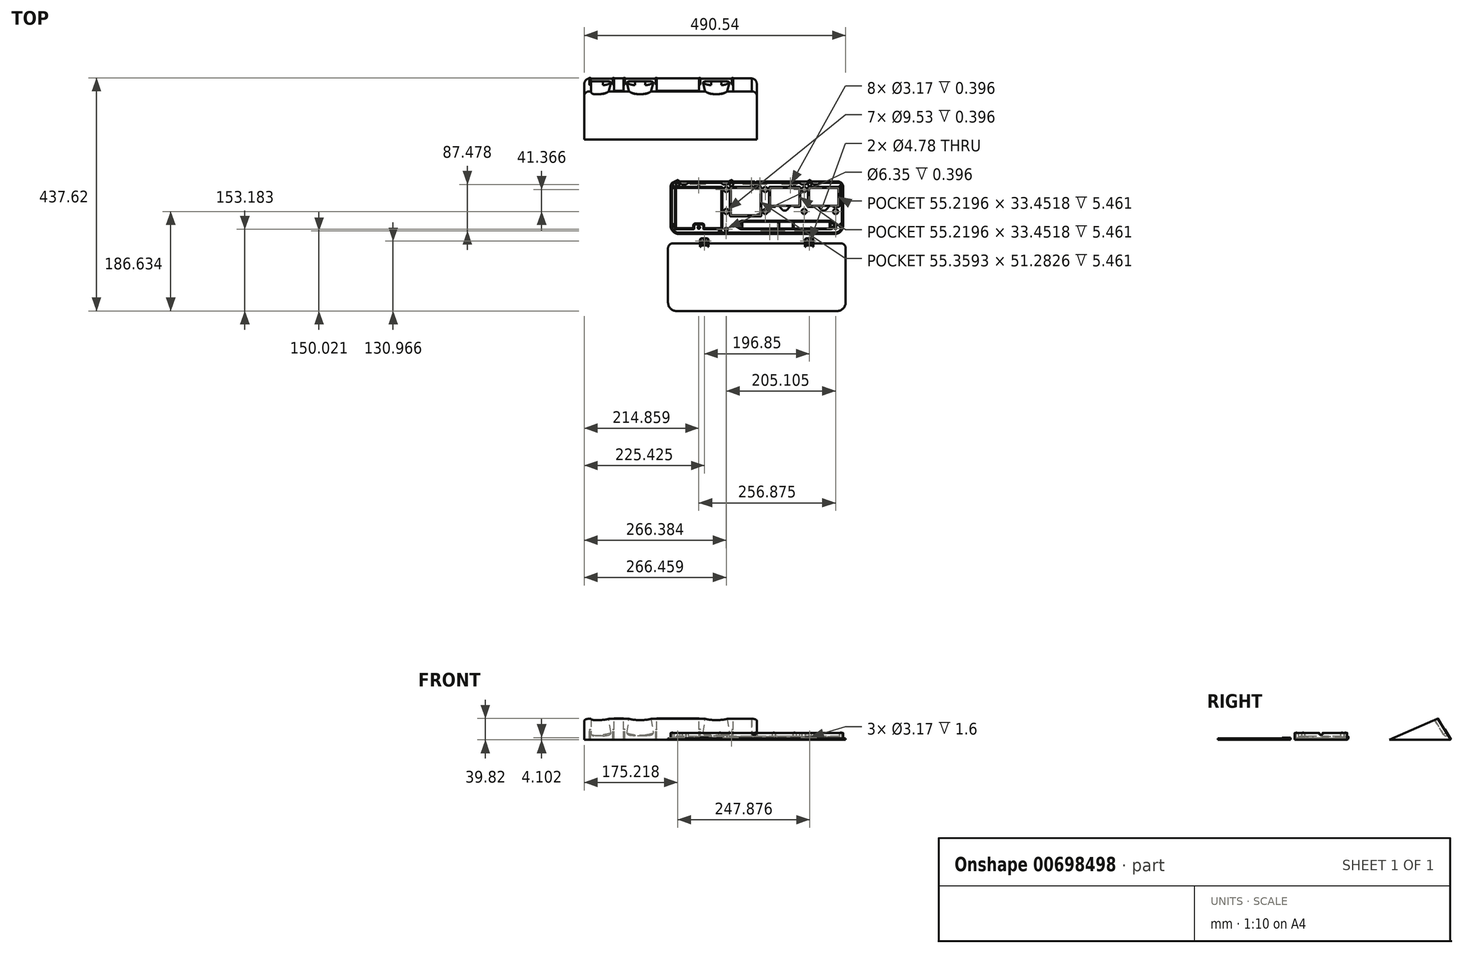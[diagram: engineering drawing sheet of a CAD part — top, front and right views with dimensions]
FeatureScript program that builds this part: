
annotation { "Feature Type Name" : "Feature", "Feature Type Description" : "" }
export const myFeature = defineFeature(function(context is Context, id is Id, definition is map)
    precondition{}
    {
        {
            var Q0;
            Q0=qCreatedBy(makeId("Top.planeOp"),FACE);
            var sketch = newSketch(context, id + "F0", { "sketchPlane" : qUnion([Q0])});
            skLineSegment(sketch, "E0.bottom", {"start": v(161.93, -49.21) * mm, "end": v(-161.93, -49.21) * mm});
            skLineSegment(sketch, "E0.top", {"start": v(161.93, 49.21) * mm, "end": v(-161.93, 49.21) * mm});
            skLineSegment(sketch, "E0.left", {"start": v(161.93, -49.21) * mm, "end": v(161.93, 49.21) * mm});
            skLineSegment(sketch, "E0.right", {"start": v(-161.93, -49.21) * mm, "end": v(-161.93, 49.21) * mm});
            skPoint(sketch, "E0.middle", {"position": v(0, 0) * mm});
            skSolve(sketch);
        }
        {
            var Q0;
            Q0=makeQuery(id+"F0.imprint","IMPRINT",FACE,{"disambiguationData":[TD([[makeQuery(id+"F0.imprint","IMPRINT",EDGE,{"derivedFrom":sQuery(id+"F0.wireOp",EDGE,"E0.bottom")}),-1.0]])]});
            extrude(context, id + "F1", {"entities" : qUnion([Q0]), "depth" : 3.17 * mm, "offsetDistance" : 25.4 * mm});
        }
        {
            var Q0;
            Q0=makeQuery(id+"F1.opExtrude","SWEPT_EDGE",EDGE,{"disambiguationData":[OSD([sQuery(id+"F0.wireOp",EDGE,"E0.bottom"),sQuery(id+"F0.wireOp",EDGE,"E0.right")])]});
            var Q1;
            Q1=makeQuery(id+"F1.opExtrude","SWEPT_EDGE",EDGE,{"disambiguationData":[OSD([sQuery(id+"F0.wireOp",EDGE,"E0.bottom"),sQuery(id+"F0.wireOp",EDGE,"E0.left")])]});
            fillet(context, id + "F2", {"entities" : qUnion([Q0, Q1]), "radius" : 15.88 * mm, "tangentPropagation" : true, "allowEdgeOverflow" : false});
        }
        {
            var Q0;
            Q0=makeQuery(id+"F1.opExtrude","SWEPT_EDGE",EDGE,{"disambiguationData":[OSD([sQuery(id+"F0.wireOp",EDGE,"E0.top"),sQuery(id+"F0.wireOp",EDGE,"E0.right")])]});
            var Q1;
            Q1=makeQuery(id+"F1.opExtrude","SWEPT_EDGE",EDGE,{"disambiguationData":[OSD([sQuery(id+"F0.wireOp",EDGE,"E0.top"),sQuery(id+"F0.wireOp",EDGE,"E0.left")])]});
            fillet(context, id + "F3", {"entities" : qUnion([Q0, Q1]), "radius" : 9.52 * mm, "tangentPropagation" : true, "allowEdgeOverflow" : false});
        }
        {
            var Q0;
            Q0=makeQuery(id+"F1.opExtrude","CAP_FACE",FACE,{"disambiguationData":[OSD([sQuery(id+"F0.wireOp",EDGE,"E0.bottom"),sQuery(id+"F0.wireOp",EDGE,"E0.top"),sQuery(id+"F0.wireOp",EDGE,"E0.left"),sQuery(id+"F0.wireOp",EDGE,"E0.right")])],"isStart":false});
            var sketch = newSketch(context, id + "F4", { "sketchPlane" : qUnion([Q0])});
            skArc(sketch, "E1.0", {"start": v(-152.4, 46.93) * mm, "mid": v(-157.52, 44.8) * mm, "end": v(-159.64, 39.69) * mm});
            skArc(sketch, "E2.0", {"start": v(-159.64, -33.34) * mm, "mid": v(-155.66, -42.95) * mm, "end": v(-146.05, -46.93) * mm});
            skLineSegment(sketch, "E3.0", {"start": v(-159.64, -33.34) * mm, "end": v(-159.64, 39.69) * mm});
            skArc(sketch, "E4.0", {"start": v(146.05, -46.93) * mm, "mid": v(155.66, -42.95) * mm, "end": v(159.64, -33.34) * mm});
            skArc(sketch, "E5.0", {"start": v(159.64, 39.69) * mm, "mid": v(157.52, 44.8) * mm, "end": v(152.4, 46.93) * mm});
            skLineSegment(sketch, "E6.0", {"start": v(159.64, -33.34) * mm, "end": v(159.64, 39.69) * mm});
            skLineSegment(sketch, "E7.0", {"start": v(152.4, 46.93) * mm, "end": v(-152.4, 46.93) * mm});
            skLineSegment(sketch, "E8.0", {"start": v(146.05, -46.93) * mm, "end": v(-146.05, -46.93) * mm});
            skSolve(sketch);
        }
        {
            var Q0;
            Q0=makeQuery(id+"F4.imprint","IMPRINT",FACE,{"disambiguationData":[TD([[makeQuery(id+"F4.imprint","IMPRINT",EDGE,{"derivedFrom":sQuery(id+"F4.wireOp",EDGE,"E1.0")}),-1.0]])]});
            extrude(context, id + "F5", {"entities" : qUnion([Q0]), "operationType" : NewBodyOperationType.ADD, "depth" : 9.52 * mm, "offsetDistance" : 25.4 * mm});
        }
        {
            var Q0;
            Q0=makeQuery(id+"F1.opExtrude","CAP_FACE",FACE,{"disambiguationData":[OSD([sQuery(id+"F0.wireOp",EDGE,"E0.bottom"),sQuery(id+"F0.wireOp",EDGE,"E0.top"),sQuery(id+"F0.wireOp",EDGE,"E0.left"),sQuery(id+"F0.wireOp",EDGE,"E0.right")])],"isStart":false});
            var sketch = newSketch(context, id + "F6", { "sketchPlane" : qUnion([Q0])});
            skCircle(sketch, "E9", {"center": v(-158.52, -33.34) * mm, "radius": 3.18 * mm});
            skLineSegment(sketch, "E10", {"start": v(-158.52, -33.34) * mm, "end": v(-158.52, 39.69) * mm, "construction": true});
            skCircle(sketch, "E11", {"center": v(-158.52, 39.69) * mm, "radius": 3.18 * mm});
            skCircle(sketch, "E12", {"center": v(158.23, 39.4) * mm, "radius": 3.18 * mm});
            skCircle(sketch, "E13", {"center": v(157.67, -33.34) * mm, "radius": 3.18 * mm});
            skCircle(sketch, "E14", {"center": v(70.74, 45.8) * mm, "radius": 3.18 * mm});
            skCircle(sketch, "E15", {"center": v(-2.29, 45.8) * mm, "radius": 3.29 * mm});
            skCircle(sketch, "E16", {"center": v(31.57, -45.8) * mm, "radius": 3.18 * mm});
            skCircle(sketch, "E17", {"center": v(-68.96, -45.8) * mm, "radius": 3.18 * mm});
            skSolve(sketch);
        }
        {
            var Q0;
            {var subQ0=sQuery(id+"F6.wireOp",EDGE,"E9");var subQ1=makeQuery(id+"F5.opExtrude","CAP_EDGE",EDGE,{"disambiguationData":[OSD([sQuery(id+"F4.wireOp",EDGE,"E2.0")])],"isStart":true});var subQ2=makeQuery(id+"F6.imprint","INTERSECT",VERTEX,{"derivedFrom":[subQ1,subQ0]});Q0=makeQuery(id+"F6.imprint","IMPRINT",FACE,{"disambiguationData":[TD([[makeQuery(id+"F6.imprint","IMPRINT",EDGE,{"disambiguationData":[TD([[subQ2,-1.0]])],"derivedFrom":subQ0}),1.0]])]});}
            var Q1;
            {var subQ0=sQuery(id+"F6.wireOp",EDGE,"E11");var subQ1=makeQuery(id+"F5.opExtrude","CAP_EDGE",EDGE,{"disambiguationData":[OSD([sQuery(id+"F4.wireOp",EDGE,"E1.0")])],"isStart":true});var subQ2=makeQuery(id+"F6.imprint","INTERSECT",VERTEX,{"derivedFrom":[subQ1,subQ0]});Q1=makeQuery(id+"F6.imprint","IMPRINT",FACE,{"disambiguationData":[TD([[makeQuery(id+"F6.imprint","IMPRINT",EDGE,{"disambiguationData":[TD([[subQ2,1.0]])],"derivedFrom":subQ0}),1.0]])]});}
            var Q2;
            {var subQ0=sQuery(id+"F6.wireOp",EDGE,"E15");var subQ1=makeQuery(id+"F5.opExtrude","CAP_EDGE",EDGE,{"disambiguationData":[OSD([sQuery(id+"F4.wireOp",EDGE,"E7.0")])],"isStart":true});var subQ2=makeQuery(id+"F6.imprint","INTERSECT",VERTEX,{"disambiguationData":[OD(0.0)],"derivedFrom":[subQ1,subQ0]});Q2=makeQuery(id+"F6.imprint","IMPRINT",FACE,{"disambiguationData":[TD([[makeQuery(id+"F6.imprint","IMPRINT",EDGE,{"disambiguationData":[TD([[subQ2,-1.0]])],"derivedFrom":subQ0}),1.0]])]});}
            var Q3;
            {var subQ0=sQuery(id+"F6.wireOp",EDGE,"E14");var subQ1=makeQuery(id+"F5.opExtrude","CAP_EDGE",EDGE,{"disambiguationData":[OSD([sQuery(id+"F4.wireOp",EDGE,"E7.0")])],"isStart":true});var subQ2=makeQuery(id+"F6.imprint","INTERSECT",VERTEX,{"disambiguationData":[OD(0.0)],"derivedFrom":[subQ1,subQ0]});Q3=makeQuery(id+"F6.imprint","IMPRINT",FACE,{"disambiguationData":[TD([[makeQuery(id+"F6.imprint","IMPRINT",EDGE,{"disambiguationData":[TD([[subQ2,1.0]])],"derivedFrom":subQ0}),1.0]])]});}
            var Q4;
            {var subQ0=sQuery(id+"F6.wireOp",EDGE,"E17");var subQ1=makeQuery(id+"F5.opExtrude","CAP_EDGE",EDGE,{"disambiguationData":[OSD([sQuery(id+"F4.wireOp",EDGE,"E8.0")])],"isStart":true});var subQ2=makeQuery(id+"F6.imprint","INTERSECT",VERTEX,{"disambiguationData":[OD(0.0)],"derivedFrom":[subQ1,subQ0]});Q4=makeQuery(id+"F6.imprint","IMPRINT",FACE,{"disambiguationData":[TD([[makeQuery(id+"F6.imprint","IMPRINT",EDGE,{"disambiguationData":[TD([[subQ2,1.0]])],"derivedFrom":subQ0}),1.0]])]});}
            var Q5;
            {var subQ0=sQuery(id+"F6.wireOp",EDGE,"E16");var subQ1=makeQuery(id+"F5.opExtrude","CAP_EDGE",EDGE,{"disambiguationData":[OSD([sQuery(id+"F4.wireOp",EDGE,"E8.0")])],"isStart":true});var subQ2=makeQuery(id+"F6.imprint","INTERSECT",VERTEX,{"disambiguationData":[OD(0.0)],"derivedFrom":[subQ1,subQ0]});Q5=makeQuery(id+"F6.imprint","IMPRINT",FACE,{"disambiguationData":[TD([[makeQuery(id+"F6.imprint","IMPRINT",EDGE,{"disambiguationData":[TD([[subQ2,-1.0]])],"derivedFrom":subQ0}),1.0]])]});}
            var Q6;
            {var subQ0=sQuery(id+"F6.wireOp",EDGE,"E13");var subQ1=makeQuery(id+"F5.opExtrude","CAP_EDGE",EDGE,{"disambiguationData":[OSD([sQuery(id+"F4.wireOp",EDGE,"E4.0")])],"isStart":true});var subQ2=makeQuery(id+"F6.imprint","INTERSECT",VERTEX,{"derivedFrom":[subQ1,subQ0]});Q6=makeQuery(id+"F6.imprint","IMPRINT",FACE,{"disambiguationData":[TD([[makeQuery(id+"F6.imprint","IMPRINT",EDGE,{"disambiguationData":[TD([[subQ2,1.0]])],"derivedFrom":subQ0}),1.0]])]});}
            var Q7;
            {var subQ0=sQuery(id+"F6.wireOp",EDGE,"E12");var subQ1=makeQuery(id+"F5.opExtrude","CAP_EDGE",EDGE,{"disambiguationData":[OSD([sQuery(id+"F4.wireOp",EDGE,"E5.0")])],"isStart":true});var subQ2=makeQuery(id+"F6.imprint","INTERSECT",VERTEX,{"derivedFrom":[subQ1,subQ0]});Q7=makeQuery(id+"F6.imprint","IMPRINT",FACE,{"disambiguationData":[TD([[makeQuery(id+"F6.imprint","IMPRINT",EDGE,{"disambiguationData":[TD([[subQ2,-1.0]])],"derivedFrom":subQ0}),1.0]])]});}
            extrude(context, id + "F7", {"entities" : qUnion([Q0, Q1, Q2, Q3, Q4, Q5, Q6, Q7]), "operationType" : NewBodyOperationType.ADD, "depth" : 9.52 * mm, "offsetDistance" : 25.4 * mm});
        }
        {
            var Q0;
            {var subQ0=sQuery(id+"F4.wireOp",EDGE,"E8.0");var subQ1=sQuery(id+"F4.wireOp",EDGE,"E7.0");var subQ2=sQuery(id+"F4.wireOp",EDGE,"E6.0");var subQ3=sQuery(id+"F4.wireOp",EDGE,"E4.0");var subQ4=sQuery(id+"F4.wireOp",EDGE,"E5.0");var subQ5=sQuery(id+"F4.wireOp",EDGE,"E3.0");var subQ6=sQuery(id+"F4.wireOp",EDGE,"E1.0");var subQ7=sQuery(id+"F4.wireOp",EDGE,"E2.0");Q0=makeQuery(id+"F7.boolean.opBoolean","MERGE",FACE,{"derivedFrom":[makeQuery(id+"F5.opExtrude","CAP_FACE",FACE,{"disambiguationData":[OSD([sQuery(id+"F0.wireOp",EDGE,"E0.bottom"),sQuery(id+"F0.wireOp",EDGE,"E0.top"),sQuery(id+"F0.wireOp",EDGE,"E0.left"),sQuery(id+"F0.wireOp",EDGE,"E0.right"),subQ6,subQ7,subQ5,subQ3,subQ4,subQ2,subQ1,subQ0])],"isStart":false}),makeQuery(id+"F7.opExtrude","CAP_FACE",FACE,{"disambiguationData":[OSD([subQ7,subQ5,sQuery(id+"F6.wireOp",EDGE,"E9")])],"isStart":false}),makeQuery(id+"F7.opExtrude","CAP_FACE",FACE,{"disambiguationData":[OSD([subQ6,subQ5,sQuery(id+"F6.wireOp",EDGE,"E11")])],"isStart":false}),makeQuery(id+"F7.opExtrude","CAP_FACE",FACE,{"disambiguationData":[OSD([subQ4,subQ2,sQuery(id+"F6.wireOp",EDGE,"E12")])],"isStart":false}),makeQuery(id+"F7.opExtrude","CAP_FACE",FACE,{"disambiguationData":[OSD([subQ3,subQ2,sQuery(id+"F6.wireOp",EDGE,"E13")])],"isStart":false}),makeQuery(id+"F7.opExtrude","CAP_FACE",FACE,{"disambiguationData":[OSD([subQ1,sQuery(id+"F6.wireOp",EDGE,"E14")])],"isStart":false}),makeQuery(id+"F7.opExtrude","CAP_FACE",FACE,{"disambiguationData":[OSD([subQ1,sQuery(id+"F6.wireOp",EDGE,"E15")])],"isStart":false}),makeQuery(id+"F7.opExtrude","CAP_FACE",FACE,{"disambiguationData":[OSD([subQ0,sQuery(id+"F6.wireOp",EDGE,"E16")])],"isStart":false}),makeQuery(id+"F7.opExtrude","CAP_FACE",FACE,{"disambiguationData":[OSD([subQ0,sQuery(id+"F6.wireOp",EDGE,"E17")])],"isStart":false})]});}
            var sketch = newSketch(context, id + "F8", { "sketchPlane" : qUnion([Q0])});
            skCircle(sketch, "E18", {"center": v(-2.29, 45.8) * mm, "radius": 1.03 * mm});
            skCircle(sketch, "E19", {"center": v(70.74, 45.8) * mm, "radius": 1.03 * mm});
            skCircle(sketch, "E20", {"center": v(158.23, 39.4) * mm, "radius": 1.03 * mm});
            skCircle(sketch, "E21", {"center": v(157.67, -33.34) * mm, "radius": 1.03 * mm});
            skCircle(sketch, "E22", {"center": v(31.57, -45.8) * mm, "radius": 1.03 * mm});
            skCircle(sketch, "E23", {"center": v(-68.96, -45.8) * mm, "radius": 1.03 * mm});
            skCircle(sketch, "E24", {"center": v(-158.52, -33.34) * mm, "radius": 1.03 * mm});
            skCircle(sketch, "E25", {"center": v(-158.52, 39.69) * mm, "radius": 1.03 * mm});
            skSolve(sketch);
        }
        {
            var Q0;
            Q0=makeQuery(id+"F8.imprint","IMPRINT",FACE,{"disambiguationData":[TD([[makeQuery(id+"F8.imprint","IMPRINT",EDGE,{"derivedFrom":sQuery(id+"F8.wireOp",EDGE,"E24")}),1.0]])]});
            var Q1;
            Q1=makeQuery(id+"F8.imprint","IMPRINT",FACE,{"disambiguationData":[TD([[makeQuery(id+"F8.imprint","IMPRINT",EDGE,{"derivedFrom":sQuery(id+"F8.wireOp",EDGE,"E23")}),1.0]])]});
            var Q2;
            Q2=makeQuery(id+"F8.imprint","IMPRINT",FACE,{"disambiguationData":[TD([[makeQuery(id+"F8.imprint","IMPRINT",EDGE,{"derivedFrom":sQuery(id+"F8.wireOp",EDGE,"E22")}),1.0]])]});
            var Q3;
            Q3=makeQuery(id+"F8.imprint","IMPRINT",FACE,{"disambiguationData":[TD([[makeQuery(id+"F8.imprint","IMPRINT",EDGE,{"derivedFrom":sQuery(id+"F8.wireOp",EDGE,"E21")}),1.0]])]});
            var Q4;
            Q4=makeQuery(id+"F8.imprint","IMPRINT",FACE,{"disambiguationData":[TD([[makeQuery(id+"F8.imprint","IMPRINT",EDGE,{"derivedFrom":sQuery(id+"F8.wireOp",EDGE,"E20")}),1.0]])]});
            var Q5;
            Q5=makeQuery(id+"F8.imprint","IMPRINT",FACE,{"disambiguationData":[TD([[makeQuery(id+"F8.imprint","IMPRINT",EDGE,{"derivedFrom":sQuery(id+"F8.wireOp",EDGE,"E19")}),1.0]])]});
            var Q6;
            Q6=makeQuery(id+"F8.imprint","IMPRINT",FACE,{"disambiguationData":[TD([[makeQuery(id+"F8.imprint","IMPRINT",EDGE,{"derivedFrom":sQuery(id+"F8.wireOp",EDGE,"E18")}),1.0]])]});
            var Q7;
            Q7=makeQuery(id+"F8.imprint","IMPRINT",FACE,{"disambiguationData":[TD([[makeQuery(id+"F8.imprint","IMPRINT",EDGE,{"derivedFrom":sQuery(id+"F8.wireOp",EDGE,"E25")}),1.0]])]});
            extrude(context, id + "F9", {"entities" : qUnion([Q0, Q1, Q2, Q3, Q4, Q5, Q6, Q7]), "operationType" : NewBodyOperationType.ADD, "depth" : 0.79 * mm, "offsetDistance" : 25.4 * mm});
        }
        {
            var Q0;
            Q0=makeQuery(id+"F1.opExtrude","CAP_FACE",FACE,{"disambiguationData":[OSD([sQuery(id+"F0.wireOp",EDGE,"E0.bottom"),sQuery(id+"F0.wireOp",EDGE,"E0.top"),sQuery(id+"F0.wireOp",EDGE,"E0.left"),sQuery(id+"F0.wireOp",EDGE,"E0.right")])],"isStart":false});
            var sketch = newSketch(context, id + "F10", { "sketchPlane" : qUnion([Q0])});
            skLineSegment(sketch, "E26", {"start": v(80.06, 46.93) * mm, "end": v(83.88, 43.75) * mm});
            skLineSegment(sketch, "E27", {"start": v(83.88, 43.75) * mm, "end": v(92.11, 43.75) * mm});
            skLineSegment(sketch, "E28", {"start": v(92.11, 43.75) * mm, "end": v(95.94, 46.93) * mm});
            skLineSegment(sketch, "E29", {"start": v(95.94, 46.93) * mm, "end": v(80.06, 46.93) * mm});
            skLineSegment(sketch, "E30", {"start": v(88, 46.93) * mm, "end": v(88, 43.23) * mm, "construction": true});
            skLineSegment(sketch, "E31", {"start": v(88, 43.75) * mm, "end": v(88, 44.46) * mm, "construction": true});
            skLineSegment(sketch, "E32", {"start": v(83.88, 45.62) * mm, "end": v(83.88, 43.16) * mm, "construction": true});
            skLineSegment(sketch, "E33", {"start": v(92.11, 45.79) * mm, "end": v(92.11, 43.52) * mm, "construction": true});
            skLineSegment(sketch, "E34", {"start": v(102.29, 46.93) * mm, "end": v(106.04, 43.75) * mm});
            skLineSegment(sketch, "E35", {"start": v(106.04, 43.75) * mm, "end": v(114.27, 43.75) * mm});
            skLineSegment(sketch, "E36", {"start": v(114.27, 43.75) * mm, "end": v(118.03, 46.93) * mm});
            skLineSegment(sketch, "E37", {"start": v(118.03, 46.93) * mm, "end": v(102.29, 46.93) * mm});
            skLineSegment(sketch, "E38", {"start": v(110.16, 46.93) * mm, "end": v(110.16, 43.75) * mm, "construction": true});
            skLineSegment(sketch, "E39", {"start": v(106.04, 45.04) * mm, "end": v(106.04, 42.78) * mm, "construction": true});
            skLineSegment(sketch, "E40", {"start": v(114.27, 44.82) * mm, "end": v(114.27, 43.03) * mm, "construction": true});
            skLineSegment(sketch, "E41", {"start": v(102.29, 47.44) * mm, "end": v(102.29, 46.4) * mm, "construction": true});
            skLineSegment(sketch, "E42", {"start": v(-67.48, 46.93) * mm, "end": v(-63.72, 43.75) * mm});
            skLineSegment(sketch, "E43", {"start": v(-63.72, 43.75) * mm, "end": v(-55.5, 43.75) * mm});
            skLineSegment(sketch, "E44", {"start": v(-55.5, 43.75) * mm, "end": v(-51.73, 46.93) * mm});
            skLineSegment(sketch, "E45", {"start": v(-51.73, 46.93) * mm, "end": v(-67.48, 46.93) * mm});
            skLineSegment(sketch, "E46", {"start": v(-59.6, 46.93) * mm, "end": v(-59.6, 41.87) * mm, "construction": true});
            skPoint(sketch, "E46.startSnap0", {"position": v(-59.6, 43.75) * mm});
            skLineSegment(sketch, "E47", {"start": v(-144.62, 46.93) * mm, "end": v(-140.86, 43.75) * mm});
            skLineSegment(sketch, "E48", {"start": v(-140.86, 43.75) * mm, "end": v(-132.63, 43.75) * mm});
            skLineSegment(sketch, "E49", {"start": v(-132.63, 43.75) * mm, "end": v(-128.87, 46.93) * mm});
            skLineSegment(sketch, "E50", {"start": v(-128.87, 46.93) * mm, "end": v(-144.62, 46.93) * mm});
            skLineSegment(sketch, "E51", {"start": v(-136.74, 46.93) * mm, "end": v(-136.74, 41.02) * mm, "construction": true});
            skSolve(sketch);
        }
        {
            var Q0;
            Q0=makeQuery(id+"F10.imprint","IMPRINT",FACE,{"disambiguationData":[TD([[makeQuery(id+"F10.imprint","IMPRINT",EDGE,{"derivedFrom":sQuery(id+"F10.wireOp",EDGE,"E47")}),1.0]])]});
            var Q1;
            Q1=makeQuery(id+"F10.imprint","IMPRINT",FACE,{"disambiguationData":[TD([[makeQuery(id+"F10.imprint","IMPRINT",EDGE,{"derivedFrom":sQuery(id+"F10.wireOp",EDGE,"E42")}),1.0]])]});
            var Q2;
            Q2=makeQuery(id+"F10.imprint","IMPRINT",FACE,{"disambiguationData":[TD([[makeQuery(id+"F10.imprint","IMPRINT",EDGE,{"derivedFrom":sQuery(id+"F10.wireOp",EDGE,"E26")}),1.0]])]});
            var Q3;
            Q3=makeQuery(id+"F10.imprint","IMPRINT",FACE,{"disambiguationData":[TD([[makeQuery(id+"F10.imprint","IMPRINT",EDGE,{"derivedFrom":sQuery(id+"F10.wireOp",EDGE,"E34")}),1.0]])]});
            extrude(context, id + "F11", {"entities" : qUnion([Q0, Q1, Q2, Q3]), "operationType" : NewBodyOperationType.ADD, "depth" : 9.52 * mm, "offsetDistance" : 25.4 * mm});
        }
        {
            var Q0;
            {var subQ0=sQuery(id+"F4.wireOp",EDGE,"E8.0");var subQ1=makeQuery(id+"F7.opExtrude","CAP_FACE",FACE,{"disambiguationData":[OSD([subQ0,sQuery(id+"F6.wireOp",EDGE,"E17")])],"isStart":false});var subQ2=makeQuery(id+"F7.opExtrude","CAP_FACE",FACE,{"disambiguationData":[OSD([subQ0,sQuery(id+"F6.wireOp",EDGE,"E16")])],"isStart":false});var subQ3=sQuery(id+"F4.wireOp",EDGE,"E7.0");var subQ4=makeQuery(id+"F7.opExtrude","CAP_FACE",FACE,{"disambiguationData":[OSD([subQ3,sQuery(id+"F6.wireOp",EDGE,"E15")])],"isStart":false});var subQ5=sQuery(id+"F6.wireOp",EDGE,"E14");var subQ6=makeQuery(id+"F7.opExtrude","CAP_FACE",FACE,{"disambiguationData":[OSD([subQ3,subQ5])],"isStart":false});var subQ7=sQuery(id+"F4.wireOp",EDGE,"E6.0");var subQ8=sQuery(id+"F4.wireOp",EDGE,"E4.0");var subQ9=makeQuery(id+"F7.opExtrude","CAP_FACE",FACE,{"disambiguationData":[OSD([subQ8,subQ7,sQuery(id+"F6.wireOp",EDGE,"E13")])],"isStart":false});var subQ11=sQuery(id+"F0.wireOp",EDGE,"E0.right");var subQ12=sQuery(id+"F0.wireOp",EDGE,"E0.left");var subQ13=sQuery(id+"F0.wireOp",EDGE,"E0.top");var subQ14=sQuery(id+"F0.wireOp",EDGE,"E0.bottom");var subQ15=makeQuery(id+"F1.opExtrude","CAP_FACE",FACE,{"disambiguationData":[OSD([subQ14,subQ13,subQ12,subQ11])],"isStart":false});var subQ16=sQuery(id+"F4.wireOp",EDGE,"E5.0");var subQ17=makeQuery(id+"F7.opExtrude","CAP_FACE",FACE,{"disambiguationData":[OSD([subQ16,subQ7,sQuery(id+"F6.wireOp",EDGE,"E12")])],"isStart":false});var subQ18=sQuery(id+"F4.wireOp",EDGE,"E3.0");var subQ19=sQuery(id+"F4.wireOp",EDGE,"E2.0");var subQ20=sQuery(id+"F4.wireOp",EDGE,"E1.0");var subQ21=makeQuery(id+"F5.opExtrude","CAP_FACE",FACE,{"disambiguationData":[OSD([subQ14,subQ13,subQ12,subQ11,subQ20,subQ19,subQ18,subQ8,subQ16,subQ7,subQ3,subQ0])],"isStart":false});var subQ22=makeQuery(id+"F7.opExtrude","CAP_FACE",FACE,{"disambiguationData":[OSD([subQ19,subQ18,sQuery(id+"F6.wireOp",EDGE,"E9")])],"isStart":false});var subQ23=makeQuery(id+"F7.opExtrude","CAP_FACE",FACE,{"disambiguationData":[OSD([subQ20,subQ18,sQuery(id+"F6.wireOp",EDGE,"E11")])],"isStart":false});var subQ24=sQuery(id+"F10.wireOp",EDGE,"E28");Q0=makeQuery(id+"F11.boolean.opBoolean","SPLIT",FACE,{"disambiguationData":[TD([makeQuery(id+"F11.opExtrude","SWEPT_FACE",FACE,{"disambiguationData":[OSD([subQ24])]})])],"derivedFrom":makeQuery(id+"F7.boolean.opBoolean","SPLIT",FACE,{"disambiguationData":[TD([subQ15,subQ21,makeQuery(id+"F5.opExtrude","SWEPT_FACE",FACE,{"disambiguationData":[OSD([subQ16])]}),subQ22,subQ23,subQ17,subQ9,makeQuery(id+"F7.opExtrude","SWEPT_FACE",FACE,{"disambiguationData":[OSD([subQ5])]}),subQ6,subQ4,subQ2,subQ1])],"derivedFrom":makeQuery(id+"F5.opExtrude","SWEPT_FACE",FACE,{"disambiguationData":[OSD([subQ3])]})})});}
            var sketch = newSketch(context, id + "F12", { "sketchPlane" : qUnion([Q0])});
            skCircle(sketch, "E52", {"center": v(-148.66, 3.04) * mm, "radius": 3.18 * mm});
            skCircle(sketch, "E53", {"center": v(99.9, 3.18) * mm, "radius": 3.18 * mm});
            skSolve(sketch);
        }
        {
            var Q0;
            Q0=makeQuery(id+"F12.imprint","IMPRINT",FACE,{"disambiguationData":[TD([[makeQuery(id+"F12.imprint","IMPRINT",EDGE,{"derivedFrom":sQuery(id+"F12.wireOp",EDGE,"E52")}),1.0]])]});
            extrude(context, id + "F13", {"entities" : qUnion([Q0]), "operationType" : NewBodyOperationType.ADD, "depth" : 6.35 * mm, "offsetDistance" : 25.4 * mm});
        }
        {
            var Q0;
            {var subQ0=sQuery(id+"F12.wireOp",EDGE,"E52");Q0=makeQuery(id+"F13.boolean.opBoolean","SPLIT",EDGE,{"disambiguationData":[TD([makeQuery(id+"F1.opExtrude","CAP_FACE",FACE,{"disambiguationData":[OSD([sQuery(id+"F0.wireOp",EDGE,"E0.bottom"),sQuery(id+"F0.wireOp",EDGE,"E0.top"),sQuery(id+"F0.wireOp",EDGE,"E0.left"),sQuery(id+"F0.wireOp",EDGE,"E0.right")])],"isStart":false})])],"derivedFrom":makeQuery(id+"F13.opExtrude","CAP_EDGE",EDGE,{"disambiguationData":[OSD([subQ0])],"isStart":false})});}
            fillet(context, id + "F14", {"entities" : qUnion([Q0]), "radius" : 2.54 * mm, "tangentPropagation" : true, "allowEdgeOverflow" : false});
        }
        {
            var Q0;
            {var subQ0=sQuery(id+"F4.wireOp",EDGE,"E8.0");var subQ1=makeQuery(id+"F7.opExtrude","CAP_FACE",FACE,{"disambiguationData":[OSD([subQ0,sQuery(id+"F6.wireOp",EDGE,"E17")])],"isStart":false});var subQ2=makeQuery(id+"F7.opExtrude","CAP_FACE",FACE,{"disambiguationData":[OSD([subQ0,sQuery(id+"F6.wireOp",EDGE,"E16")])],"isStart":false});var subQ3=sQuery(id+"F4.wireOp",EDGE,"E7.0");var subQ4=makeQuery(id+"F7.opExtrude","CAP_FACE",FACE,{"disambiguationData":[OSD([subQ3,sQuery(id+"F6.wireOp",EDGE,"E15")])],"isStart":false});var subQ5=sQuery(id+"F6.wireOp",EDGE,"E14");var subQ6=makeQuery(id+"F7.opExtrude","CAP_FACE",FACE,{"disambiguationData":[OSD([subQ3,subQ5])],"isStart":false});var subQ7=sQuery(id+"F4.wireOp",EDGE,"E6.0");var subQ8=sQuery(id+"F4.wireOp",EDGE,"E4.0");var subQ9=makeQuery(id+"F7.opExtrude","CAP_FACE",FACE,{"disambiguationData":[OSD([subQ8,subQ7,sQuery(id+"F6.wireOp",EDGE,"E13")])],"isStart":false});var subQ11=sQuery(id+"F0.wireOp",EDGE,"E0.right");var subQ12=sQuery(id+"F0.wireOp",EDGE,"E0.left");var subQ13=sQuery(id+"F0.wireOp",EDGE,"E0.top");var subQ14=sQuery(id+"F0.wireOp",EDGE,"E0.bottom");var subQ15=makeQuery(id+"F1.opExtrude","CAP_FACE",FACE,{"disambiguationData":[OSD([subQ14,subQ13,subQ12,subQ11])],"isStart":false});var subQ16=sQuery(id+"F4.wireOp",EDGE,"E5.0");var subQ17=makeQuery(id+"F7.opExtrude","CAP_FACE",FACE,{"disambiguationData":[OSD([subQ16,subQ7,sQuery(id+"F6.wireOp",EDGE,"E12")])],"isStart":false});var subQ18=sQuery(id+"F4.wireOp",EDGE,"E3.0");var subQ19=sQuery(id+"F4.wireOp",EDGE,"E2.0");var subQ20=sQuery(id+"F4.wireOp",EDGE,"E1.0");var subQ21=makeQuery(id+"F5.opExtrude","CAP_FACE",FACE,{"disambiguationData":[OSD([subQ14,subQ13,subQ12,subQ11,subQ20,subQ19,subQ18,subQ8,subQ16,subQ7,subQ3,subQ0])],"isStart":false});var subQ22=makeQuery(id+"F7.opExtrude","CAP_FACE",FACE,{"disambiguationData":[OSD([subQ19,subQ18,sQuery(id+"F6.wireOp",EDGE,"E9")])],"isStart":false});var subQ23=makeQuery(id+"F7.opExtrude","CAP_FACE",FACE,{"disambiguationData":[OSD([subQ20,subQ18,sQuery(id+"F6.wireOp",EDGE,"E11")])],"isStart":false});var subQ24=sQuery(id+"F10.wireOp",EDGE,"E28");Q0=makeQuery(id+"F11.boolean.opBoolean","SPLIT",FACE,{"disambiguationData":[TD([makeQuery(id+"F11.opExtrude","SWEPT_FACE",FACE,{"disambiguationData":[OSD([subQ24])]})])],"derivedFrom":makeQuery(id+"F7.boolean.opBoolean","SPLIT",FACE,{"disambiguationData":[TD([subQ15,subQ21,makeQuery(id+"F5.opExtrude","SWEPT_FACE",FACE,{"disambiguationData":[OSD([subQ16])]}),subQ22,subQ23,subQ17,subQ9,makeQuery(id+"F7.opExtrude","SWEPT_FACE",FACE,{"disambiguationData":[OSD([subQ5])]}),subQ6,subQ4,subQ2,subQ1])],"derivedFrom":makeQuery(id+"F5.opExtrude","SWEPT_FACE",FACE,{"disambiguationData":[OSD([subQ3])]})})});}
            var sketch = newSketch(context, id + "F15", { "sketchPlane" : qUnion([Q0])});
            skCircle(sketch, "E54", {"center": v(99.11, 3.18) * mm, "radius": 2.92 * mm});
            skSolve(sketch);
        }
        {
            var Q0;
            {var subQ0=sQuery(id+"F15.wireOp",EDGE,"E54");var subQ1=makeQuery(id+"F1.opExtrude","CAP_FACE",FACE,{"disambiguationData":[OSD([sQuery(id+"F0.wireOp",EDGE,"E0.bottom"),sQuery(id+"F0.wireOp",EDGE,"E0.top"),sQuery(id+"F0.wireOp",EDGE,"E0.left"),sQuery(id+"F0.wireOp",EDGE,"E0.right")])],"isStart":false});var subQ2=sQuery(id+"F4.wireOp",EDGE,"E7.0");var subQ3=makeQuery(id+"F5.opExtrude","SWEPT_FACE",FACE,{"disambiguationData":[OSD([subQ2])]});var subQ4=makeQuery(id+"F11.boolean.opBoolean","SPLIT",EDGE,{"disambiguationData":[TD([makeQuery(id+"F11.opExtrude","SWEPT_FACE",FACE,{"disambiguationData":[OSD([sQuery(id+"F10.wireOp",EDGE,"E28")])]})])],"derivedFrom":makeQuery(id+"F7.boolean.opBoolean","SPLIT",EDGE,{"disambiguationData":[TD([subQ1,makeQuery(id+"F5.opExtrude","SWEPT_FACE",FACE,{"disambiguationData":[OSD([sQuery(id+"F4.wireOp",EDGE,"E5.0")])]}),subQ3,makeQuery(id+"F7.opExtrude","SWEPT_FACE",FACE,{"disambiguationData":[OSD([sQuery(id+"F6.wireOp",EDGE,"E14")])]})])],"derivedFrom":makeQuery(id+"F5.opExtrude","CAP_EDGE",EDGE,{"disambiguationData":[OSD([subQ2])],"isStart":true})})});var subQ5=makeQuery(id+"F15.imprint","INTERSECT",VERTEX,{"disambiguationData":[OD(0.0)],"derivedFrom":[subQ4,subQ0]});Q0=makeQuery(id+"F15.imprint","IMPRINT",FACE,{"disambiguationData":[TD([[makeQuery(id+"F15.imprint","IMPRINT",EDGE,{"disambiguationData":[TD([[subQ5,1.0]])],"derivedFrom":subQ0}),1.0]])]});}
            var Q1;
            Q1=sQuery(id+"F15.wireOp",EDGE,"E54");
            extrude(context, id + "F16", {"entities" : qUnion([Q0]), "operationType" : NewBodyOperationType.ADD, "surfaceEntities" : qUnion([Q1]), "depth" : 6.35 * mm, "offsetDistance" : 25.4 * mm});
        }
        {
            var Q0;
            Q0=makeQuery(id+"F16.opExtrude","CAP_EDGE",EDGE,{"disambiguationData":[OSD([sQuery(id+"F15.wireOp",EDGE,"E54")])],"isStart":false});
            fillet(context, id + "F17", {"entities" : qUnion([Q0]), "radius" : 2.54 * mm, "tangentPropagation" : true, "allowEdgeOverflow" : false});
        }
        {
            var Q0;
            {var subQ0=sQuery(id+"F4.wireOp",EDGE,"E8.0");var subQ1=makeQuery(id+"F7.opExtrude","CAP_FACE",FACE,{"disambiguationData":[OSD([subQ0,sQuery(id+"F6.wireOp",EDGE,"E16")])],"isStart":false});var subQ2=sQuery(id+"F6.wireOp",EDGE,"E15");var subQ3=sQuery(id+"F4.wireOp",EDGE,"E7.0");var subQ4=makeQuery(id+"F7.opExtrude","CAP_FACE",FACE,{"disambiguationData":[OSD([subQ3,subQ2])],"isStart":false});var subQ6=makeQuery(id+"F7.opExtrude","SWEPT_FACE",FACE,{"disambiguationData":[OSD([subQ2])]});var subQ7=makeQuery(id+"F7.opExtrude","CAP_FACE",FACE,{"disambiguationData":[OSD([subQ3,sQuery(id+"F6.wireOp",EDGE,"E14")])],"isStart":false});var subQ8=sQuery(id+"F4.wireOp",EDGE,"E6.0");var subQ9=sQuery(id+"F4.wireOp",EDGE,"E4.0");var subQ10=makeQuery(id+"F7.opExtrude","CAP_FACE",FACE,{"disambiguationData":[OSD([subQ9,subQ8,sQuery(id+"F6.wireOp",EDGE,"E13")])],"isStart":false});var subQ11=sQuery(id+"F0.wireOp",EDGE,"E0.right");var subQ12=sQuery(id+"F0.wireOp",EDGE,"E0.left");var subQ13=sQuery(id+"F0.wireOp",EDGE,"E0.top");var subQ14=sQuery(id+"F0.wireOp",EDGE,"E0.bottom");var subQ15=makeQuery(id+"F1.opExtrude","CAP_FACE",FACE,{"disambiguationData":[OSD([subQ14,subQ13,subQ12,subQ11])],"isStart":false});var subQ16=sQuery(id+"F4.wireOp",EDGE,"E5.0");var subQ17=makeQuery(id+"F7.opExtrude","CAP_FACE",FACE,{"disambiguationData":[OSD([subQ16,subQ8,sQuery(id+"F6.wireOp",EDGE,"E12")])],"isStart":false});var subQ18=sQuery(id+"F4.wireOp",EDGE,"E3.0");var subQ19=sQuery(id+"F4.wireOp",EDGE,"E2.0");var subQ20=sQuery(id+"F4.wireOp",EDGE,"E1.0");var subQ21=makeQuery(id+"F5.opExtrude","CAP_FACE",FACE,{"disambiguationData":[OSD([subQ14,subQ13,subQ12,subQ11,subQ20,subQ19,subQ18,subQ9,subQ16,subQ8,subQ3,subQ0])],"isStart":false});var subQ22=makeQuery(id+"F7.opExtrude","CAP_FACE",FACE,{"disambiguationData":[OSD([subQ19,subQ18,sQuery(id+"F6.wireOp",EDGE,"E9")])],"isStart":false});var subQ23=makeQuery(id+"F7.opExtrude","CAP_FACE",FACE,{"disambiguationData":[OSD([subQ20,subQ18,sQuery(id+"F6.wireOp",EDGE,"E11")])],"isStart":false});var subQ24=makeQuery(id+"F7.opExtrude","CAP_FACE",FACE,{"disambiguationData":[OSD([subQ0,sQuery(id+"F6.wireOp",EDGE,"E17")])],"isStart":false});Q0=makeQuery(id+"F11.boolean.opBoolean","SPLIT",FACE,{"disambiguationData":[TD([subQ6])],"derivedFrom":makeQuery(id+"F7.boolean.opBoolean","SPLIT",FACE,{"disambiguationData":[TD([subQ15,makeQuery(id+"F5.opExtrude","SWEPT_FACE",FACE,{"disambiguationData":[OSD([subQ20])]}),subQ21,subQ22,subQ23,subQ17,subQ10,subQ7,subQ6,subQ4,subQ1,subQ24])],"derivedFrom":makeQuery(id+"F5.opExtrude","SWEPT_FACE",FACE,{"disambiguationData":[OSD([subQ3])]})})});}
            var sketch = newSketch(context, id + "F18", { "sketchPlane" : qUnion([Q0])});
            skCircle(sketch, "E55", {"center": v(-47.86, 3.18) * mm, "radius": 3.18 * mm});
            skSolve(sketch);
        }
        {
            var Q0;
            {var subQ0=sQuery(id+"F18.wireOp",EDGE,"E55");var subQ1=makeQuery(id+"F1.opExtrude","CAP_FACE",FACE,{"disambiguationData":[OSD([sQuery(id+"F0.wireOp",EDGE,"E0.bottom"),sQuery(id+"F0.wireOp",EDGE,"E0.top"),sQuery(id+"F0.wireOp",EDGE,"E0.left"),sQuery(id+"F0.wireOp",EDGE,"E0.right")])],"isStart":false});var subQ2=sQuery(id+"F4.wireOp",EDGE,"E7.0");var subQ3=makeQuery(id+"F5.opExtrude","SWEPT_FACE",FACE,{"disambiguationData":[OSD([subQ2])]});var subQ4=makeQuery(id+"F7.opExtrude","SWEPT_FACE",FACE,{"disambiguationData":[OSD([sQuery(id+"F6.wireOp",EDGE,"E15")])]});var subQ5=makeQuery(id+"F11.boolean.opBoolean","SPLIT",EDGE,{"disambiguationData":[TD([subQ4])],"derivedFrom":makeQuery(id+"F7.boolean.opBoolean","SPLIT",EDGE,{"disambiguationData":[TD([subQ1,makeQuery(id+"F5.opExtrude","SWEPT_FACE",FACE,{"disambiguationData":[OSD([sQuery(id+"F4.wireOp",EDGE,"E1.0")])]}),subQ3,subQ4])],"derivedFrom":makeQuery(id+"F5.opExtrude","CAP_EDGE",EDGE,{"disambiguationData":[OSD([subQ2])],"isStart":true})})});var subQ6=makeQuery(id+"F18.imprint","INTERSECT",VERTEX,{"disambiguationData":[OD(0.0)],"derivedFrom":[subQ5,subQ0]});Q0=makeQuery(id+"F18.imprint","IMPRINT",FACE,{"disambiguationData":[TD([[makeQuery(id+"F18.imprint","IMPRINT",EDGE,{"disambiguationData":[TD([[subQ6,-1.0]])],"derivedFrom":subQ0}),1.0]])]});}
            extrude(context, id + "F19", {"entities" : qUnion([Q0]), "operationType" : NewBodyOperationType.ADD, "depth" : 6.35 * mm, "offsetDistance" : 25.4 * mm});
        }
        {
            var Q0;
            Q0=makeQuery(id+"F19.opExtrude","CAP_EDGE",EDGE,{"disambiguationData":[OSD([sQuery(id+"F18.wireOp",EDGE,"E55")])],"isStart":false});
            fillet(context, id + "F20", {"entities" : qUnion([Q0]), "radius" : 2.54 * mm, "tangentPropagation" : true, "allowEdgeOverflow" : false});
        }
        {
            var Q0;
            Q0=makeQuery(id+"F1.opExtrude","CAP_FACE",FACE,{"disambiguationData":[OSD([sQuery(id+"F0.wireOp",EDGE,"E0.bottom"),sQuery(id+"F0.wireOp",EDGE,"E0.top"),sQuery(id+"F0.wireOp",EDGE,"E0.left"),sQuery(id+"F0.wireOp",EDGE,"E0.right")])],"isStart":false});
            var sketch = newSketch(context, id + "F21", { "sketchPlane" : qUnion([Q0])});
            skLineSegment(sketch, "E56.bottom", {"start": v(154.86, 38.99) * mm, "end": v(95.94, 38.99) * mm});
            skLineSegment(sketch, "E56.top", {"start": v(154.86, 1.83) * mm, "end": v(95.94, 1.83) * mm});
            skLineSegment(sketch, "E56.left", {"start": v(154.86, 38.99) * mm, "end": v(154.86, 1.83) * mm});
            skLineSegment(sketch, "E56.right", {"start": v(95.94, 38.99) * mm, "end": v(95.94, 1.83) * mm});
            skPoint(sketch, "E57.MirrorCS.start.orphan", {"position": v(95.94, 38.99) * mm});
            skPoint(sketch, "E58.MirrorCS.start.orphan", {"position": v(154.86, 38.99) * mm});
            skSolve(sketch);
        }
        {
            var Q0;
            Q0=makeQuery(id+"F21.imprint","IMPRINT",FACE,{"disambiguationData":[TD([[makeQuery(id+"F21.imprint","IMPRINT",EDGE,{"derivedFrom":sQuery(id+"F21.wireOp",EDGE,"E56.bottom")}),1.0]])]});
            extrude(context, id + "F22", {"entities" : qUnion([Q0]), "operationType" : NewBodyOperationType.ADD, "depth" : 2.83 * mm, "offsetDistance" : 25.4 * mm});
        }
        {
            var Q0;
            Q0=makeQuery(id+"F22.opExtrude","SWEPT_EDGE",EDGE,{"disambiguationData":[OSD([sQuery(id+"F21.wireOp",EDGE,"E56.top"),sQuery(id+"F21.wireOp",EDGE,"E56.right")])]});
            var Q1;
            Q1=makeQuery(id+"F22.opExtrude","SWEPT_EDGE",EDGE,{"disambiguationData":[OSD([sQuery(id+"F21.wireOp",EDGE,"E56.bottom"),sQuery(id+"F21.wireOp",EDGE,"E56.right")])]});
            var Q2;
            Q2=makeQuery(id+"F22.opExtrude","SWEPT_EDGE",EDGE,{"disambiguationData":[OSD([sQuery(id+"F21.wireOp",EDGE,"E56.bottom"),sQuery(id+"F21.wireOp",EDGE,"E56.left")])]});
            var Q3;
            Q3=makeQuery(id+"F22.opExtrude","SWEPT_EDGE",EDGE,{"disambiguationData":[OSD([sQuery(id+"F21.wireOp",EDGE,"E56.top"),sQuery(id+"F21.wireOp",EDGE,"E56.left")])]});
            fillet(context, id + "F23", {"entities" : qUnion([Q0, Q1, Q2, Q3]), "radius" : 1.27 * mm, "tangentPropagation" : true, "allowEdgeOverflow" : false});
        }
        {
            var Q0;
            Q0=makeQuery(id+"F22.opExtrude","CAP_FACE",FACE,{"disambiguationData":[OSD([sQuery(id+"F21.wireOp",EDGE,"E56.bottom"),sQuery(id+"F21.wireOp",EDGE,"E56.top"),sQuery(id+"F21.wireOp",EDGE,"E56.left"),sQuery(id+"F21.wireOp",EDGE,"E56.right")])],"isStart":false});
            var sketch = newSketch(context, id + "F24", { "sketchPlane" : qUnion([Q0])});
            skLineSegment(sketch, "E59.0", {"start": v(97.79, 3.68) * mm, "end": v(153, 3.68) * mm});
            skLineSegment(sketch, "E59.1", {"start": v(97.79, 37.13) * mm, "end": v(97.79, 3.68) * mm});
            skLineSegment(sketch, "E59.2", {"start": v(153, 37.13) * mm, "end": v(97.79, 37.13) * mm});
            skLineSegment(sketch, "E59.3", {"start": v(153, 3.68) * mm, "end": v(153, 37.13) * mm});
            skSolve(sketch);
        }
        {
            var Q0;
            Q0=makeQuery(id+"F24.imprint","IMPRINT",FACE,{"disambiguationData":[TD([[makeQuery(id+"F24.imprint","IMPRINT",EDGE,{"derivedFrom":sQuery(id+"F24.wireOp",EDGE,"E59.0")}),1.0]])]});
            extrude(context, id + "F25", {"entities" : qUnion([Q0]), "operationType" : NewBodyOperationType.REMOVE, "oppositeDirection" : true, "depth" : 5.7 * mm, "offsetDistance" : 25.4 * mm});
        }
        {
            var Q0;
            Q0=makeQuery(id+"F1.opExtrude","CAP_FACE",FACE,{"disambiguationData":[OSD([sQuery(id+"F0.wireOp",EDGE,"E0.bottom"),sQuery(id+"F0.wireOp",EDGE,"E0.top"),sQuery(id+"F0.wireOp",EDGE,"E0.left"),sQuery(id+"F0.wireOp",EDGE,"E0.right")])],"isStart":false});
            var sketch = newSketch(context, id + "F26", { "sketchPlane" : qUnion([Q0])});
            skLineSegment(sketch, "E60.bottom", {"start": v(81.65, 38.98) * mm, "end": v(22.72, 38.98) * mm});
            skLineSegment(sketch, "E60.top", {"start": v(81.65, 1.82) * mm, "end": v(22.72, 1.82) * mm});
            skLineSegment(sketch, "E60.left", {"start": v(81.65, 38.98) * mm, "end": v(81.65, 1.82) * mm});
            skLineSegment(sketch, "E60.right", {"start": v(22.72, 38.98) * mm, "end": v(22.72, 1.82) * mm});
            skSolve(sketch);
        }
        {
            var Q0;
            Q0=makeQuery(id+"F26.imprint","IMPRINT",FACE,{"disambiguationData":[TD([[makeQuery(id+"F26.imprint","IMPRINT",EDGE,{"derivedFrom":sQuery(id+"F26.wireOp",EDGE,"E60.bottom")}),1.0]])]});
            extrude(context, id + "F27", {"entities" : qUnion([Q0]), "operationType" : NewBodyOperationType.ADD, "depth" : 2.84 * mm, "offsetDistance" : 25.4 * mm});
        }
        {
            var Q0;
            Q0=makeQuery(id+"F27.opExtrude","SWEPT_EDGE",EDGE,{"disambiguationData":[OSD([sQuery(id+"F26.wireOp",EDGE,"E60.top"),sQuery(id+"F26.wireOp",EDGE,"E60.right")])]});
            var Q1;
            Q1=makeQuery(id+"F27.opExtrude","SWEPT_EDGE",EDGE,{"disambiguationData":[OSD([sQuery(id+"F26.wireOp",EDGE,"E60.top"),sQuery(id+"F26.wireOp",EDGE,"E60.left")])]});
            var Q2;
            Q2=makeQuery(id+"F27.opExtrude","SWEPT_EDGE",EDGE,{"disambiguationData":[OSD([sQuery(id+"F26.wireOp",EDGE,"E60.bottom"),sQuery(id+"F26.wireOp",EDGE,"E60.left")])]});
            var Q3;
            Q3=makeQuery(id+"F27.opExtrude","SWEPT_EDGE",EDGE,{"disambiguationData":[OSD([sQuery(id+"F26.wireOp",EDGE,"E60.bottom"),sQuery(id+"F26.wireOp",EDGE,"E60.right")])]});
            fillet(context, id + "F28", {"entities" : qUnion([Q0, Q1, Q2, Q3]), "radius" : 1.27 * mm, "tangentPropagation" : true, "allowEdgeOverflow" : false});
        }
        {
            var Q0;
            Q0=makeQuery(id+"F27.opExtrude","CAP_FACE",FACE,{"disambiguationData":[OSD([sQuery(id+"F26.wireOp",EDGE,"E60.bottom"),sQuery(id+"F26.wireOp",EDGE,"E60.top"),sQuery(id+"F26.wireOp",EDGE,"E60.left"),sQuery(id+"F26.wireOp",EDGE,"E60.right")])],"isStart":false});
            var sketch = newSketch(context, id + "F29", { "sketchPlane" : qUnion([Q0])});
            skLineSegment(sketch, "E61.0", {"start": v(24.57, 3.67) * mm, "end": v(79.8, 3.67) * mm});
            skLineSegment(sketch, "E61.1", {"start": v(24.57, 37.12) * mm, "end": v(24.57, 3.67) * mm});
            skLineSegment(sketch, "E61.2", {"start": v(79.8, 37.12) * mm, "end": v(24.57, 37.12) * mm});
            skLineSegment(sketch, "E61.3", {"start": v(79.8, 3.67) * mm, "end": v(79.8, 37.12) * mm});
            skSolve(sketch);
        }
        {
            var Q0;
            Q0=makeQuery(id+"F29.imprint","IMPRINT",FACE,{"disambiguationData":[TD([[makeQuery(id+"F29.imprint","IMPRINT",EDGE,{"derivedFrom":sQuery(id+"F29.wireOp",EDGE,"E61.0")}),1.0]])]});
            extrude(context, id + "F30", {"entities" : qUnion([Q0]), "operationType" : NewBodyOperationType.REMOVE, "oppositeDirection" : true, "depth" : 5.7 * mm, "offsetDistance" : 25.4 * mm});
        }
        {
            var Q0;
            Q0=makeQuery(id+"F22.opExtrude","SWEPT_FACE",FACE,{"disambiguationData":[OSD([sQuery(id+"F21.wireOp",EDGE,"E56.top")])]});
            var sketch = newSketch(context, id + "F31", { "sketchPlane" : qUnion([Q0])});
            skLineSegment(sketch, "E62.bottom", {"start": v(103.17, 3.18) * mm, "end": v(147.62, 3.18) * mm});
            skLineSegment(sketch, "E62.top", {"start": v(103.17, 17.48) * mm, "end": v(147.62, 17.48) * mm});
            skLineSegment(sketch, "E62.left", {"start": v(103.17, 3.17) * mm, "end": v(103.17, 17.48) * mm});
            skLineSegment(sketch, "E62.right", {"start": v(147.62, 3.18) * mm, "end": v(147.62, 17.48) * mm});
            skLineSegment(sketch, "E63", {"start": v(125.4, 6) * mm, "end": v(124.34, 16.54) * mm, "construction": true});
            skLineSegment(sketch, "E64", {"start": v(125.4, 17.48) * mm, "end": v(125.4, 3.18) * mm, "construction": true});
            skSolve(sketch);
        }
        {
            var Q0;
            Q0=makeQuery(id+"F27.opExtrude","SWEPT_FACE",FACE,{"disambiguationData":[OSD([sQuery(id+"F26.wireOp",EDGE,"E60.top")])]});
            var sketch = newSketch(context, id + "F32", { "sketchPlane" : qUnion([Q0])});
            skLineSegment(sketch, "E65.bottom", {"start": v(29.96, 3.18) * mm, "end": v(74.4, 3.18) * mm});
            skLineSegment(sketch, "E65.top", {"start": v(29.96, 17.48) * mm, "end": v(74.4, 17.48) * mm});
            skLineSegment(sketch, "E65.left", {"start": v(29.96, 3.17) * mm, "end": v(29.96, 17.48) * mm});
            skLineSegment(sketch, "E65.right", {"start": v(74.4, 3.18) * mm, "end": v(74.4, 17.48) * mm});
            skPoint(sketch, "E66.orphan", {"position": v(52.18, 17.48) * mm});
            skPoint(sketch, "E67.start.orphan", {"position": v(52.18, 3.18) * mm});
            skSolve(sketch);
        }
        {
            var Q0;
            {var subQ0=sQuery(id+"F31.wireOp",EDGE,"E62.top");Q0=makeQuery(id+"F31.imprint","IMPRINT",FACE,{"disambiguationData":[TD([[makeQuery(id+"F31.imprint","IMPRINT",EDGE,{"derivedFrom":subQ0}),-1.0]])]});}
            var Q1;
            {var subQ0=sQuery(id+"F32.wireOp",EDGE,"E65.top");Q1=makeQuery(id+"F32.imprint","IMPRINT",FACE,{"disambiguationData":[TD([[makeQuery(id+"F32.imprint","IMPRINT",EDGE,{"derivedFrom":subQ0}),-1.0]])]});}
            extrude(context, id + "F33", {"entities" : qUnion([Q0, Q1]), "operationType" : NewBodyOperationType.ADD, "oppositeDirection" : true, "depth" : 2.3 * mm, "offsetDistance" : 25.4 * mm});
        }
        {
            var Q0;
            {var subQ0=sQuery(id+"F21.wireOp",EDGE,"E56.top");Q0=makeQuery(id+"F33.boolean.opBoolean","MERGE",FACE,{"derivedFrom":[makeQuery(id+"F22.opExtrude","SWEPT_FACE",FACE,{"disambiguationData":[OSD([subQ0])]}),makeQuery(id+"F33.opExtrude","CAP_FACE",FACE,{"disambiguationData":[OSD([subQ0,sQuery(id+"F31.wireOp",EDGE,"E62.top"),sQuery(id+"F31.wireOp",EDGE,"E62.left"),sQuery(id+"F31.wireOp",EDGE,"E62.right")])],"isStart":true})]});}
            var sketch = newSketch(context, id + "F34", { "sketchPlane" : qUnion([Q0])});
            skArc(sketch, "E68", {"start": v(103.17, 6) * mm, "mid": v(105.54, 3.9) * mm, "end": v(108.64, 3.17) * mm});
            skArc(sketch, "E69", {"start": v(142.16, 3.18) * mm, "mid": v(145.26, 3.9) * mm, "end": v(147.62, 6) * mm});
            skLineSegment(sketch, "E70", {"start": v(108.64, 3.17) * mm, "end": v(142.16, 3.18) * mm});
            skLineSegment(sketch, "E71", {"start": v(147.62, 6) * mm, "end": v(147.62, 17.48) * mm});
            skLineSegment(sketch, "E72", {"start": v(147.62, 17.48) * mm, "end": v(103.17, 17.48) * mm});
            skLineSegment(sketch, "E73", {"start": v(103.17, 17.48) * mm, "end": v(103.17, 6) * mm});
            skSolve(sketch);
        }
        {
            var Q0;
            {var subQ0=sQuery(id+"F26.wireOp",EDGE,"E60.top");Q0=makeQuery(id+"F33.boolean.opBoolean","MERGE",FACE,{"derivedFrom":[makeQuery(id+"F27.opExtrude","SWEPT_FACE",FACE,{"disambiguationData":[OSD([subQ0])]}),makeQuery(id+"F33.opExtrude","CAP_FACE",FACE,{"disambiguationData":[OSD([subQ0,sQuery(id+"F32.wireOp",EDGE,"E65.top"),sQuery(id+"F32.wireOp",EDGE,"E65.left"),sQuery(id+"F32.wireOp",EDGE,"E65.right")])],"isStart":true})]});}
            var sketch = newSketch(context, id + "F35", { "sketchPlane" : qUnion([Q0])});
            skPoint(sketch, "E74.end.orphan", {"position": v(35.42, 3.18) * mm});
            skArc(sketch, "E75", {"start": v(29.96, 6.02) * mm, "mid": v(32.33, 3.9) * mm, "end": v(35.42, 3.17) * mm});
            skPoint(sketch, "E76.start.orphan", {"position": v(68.95, 3.18) * mm});
            skArc(sketch, "E77", {"start": v(68.95, 3.18) * mm, "mid": v(72.04, 3.9) * mm, "end": v(74.4, 6.02) * mm});
            skLineSegment(sketch, "E78", {"start": v(35.42, 3.18) * mm, "end": v(68.95, 3.18) * mm});
            skLineSegment(sketch, "E79", {"start": v(74.4, 6.02) * mm, "end": v(74.4, 17.48) * mm});
            skLineSegment(sketch, "E80", {"start": v(74.4, 17.48) * mm, "end": v(29.96, 17.48) * mm});
            skLineSegment(sketch, "E81", {"start": v(29.96, 17.48) * mm, "end": v(29.96, 6.02) * mm});
            skSolve(sketch);
        }
        {
            var Q0;
            {var subQ0=sQuery(id+"F35.wireOp",EDGE,"E78");Q0=makeQuery(id+"F35.imprint","IMPRINT",FACE,{"disambiguationData":[TD([[makeQuery(id+"F35.imprint","IMPRINT",EDGE,{"derivedFrom":subQ0}),-1.0]])]});}
            extrude(context, id + "F36", {"entities" : qUnion([Q0]), "operationType" : NewBodyOperationType.REMOVE, "oppositeDirection" : true, "depth" : 2.54 * mm, "offsetDistance" : 25.4 * mm});
        }
        {
            var Q0;
            {var subQ0=sQuery(id+"F34.wireOp",EDGE,"E70");Q0=makeQuery(id+"F34.imprint","IMPRINT",FACE,{"disambiguationData":[TD([[makeQuery(id+"F34.imprint","IMPRINT",EDGE,{"derivedFrom":subQ0}),-1.0]])]});}
            extrude(context, id + "F37", {"entities" : qUnion([Q0]), "operationType" : NewBodyOperationType.REMOVE, "oppositeDirection" : true, "depth" : 2.54 * mm, "offsetDistance" : 25.4 * mm});
        }
        {
            var Q0;
            Q0=makeQuery(id+"F37.boolean.opBoolean","MERGE",FACE,{"derivedFrom":[makeQuery(id+"F36.boolean.opBoolean","MERGE",FACE,{"derivedFrom":[makeQuery(id+"F1.opExtrude","CAP_FACE",FACE,{"disambiguationData":[OSD([sQuery(id+"F0.wireOp",EDGE,"E0.bottom"),sQuery(id+"F0.wireOp",EDGE,"E0.top"),sQuery(id+"F0.wireOp",EDGE,"E0.left"),sQuery(id+"F0.wireOp",EDGE,"E0.right")])],"isStart":false}),makeQuery(id+"F36.opExtrude","SWEPT_FACE",FACE,{"disambiguationData":[OSD([sQuery(id+"F26.wireOp",EDGE,"E60.top"),sQuery(id+"F35.wireOp",EDGE,"E78")])]})]}),makeQuery(id+"F37.opExtrude","SWEPT_FACE",FACE,{"disambiguationData":[OSD([sQuery(id+"F21.wireOp",EDGE,"E56.top"),sQuery(id+"F34.wireOp",EDGE,"E70")])]})]});
            var sketch = newSketch(context, id + "F38", { "sketchPlane" : qUnion([Q0])});
            skLineSegment(sketch, "E82.bottom", {"start": v(8.62, 38.98) * mm, "end": v(-50.44, 38.98) * mm});
            skLineSegment(sketch, "E82.top", {"start": v(8.62, -16.01) * mm, "end": v(-50.44, -16.01) * mm});
            skLineSegment(sketch, "E82.left", {"start": v(8.62, 38.98) * mm, "end": v(8.62, -16.01) * mm});
            skLineSegment(sketch, "E82.right", {"start": v(-50.44, 38.98) * mm, "end": v(-50.44, -16.01) * mm});
            skSolve(sketch);
        }
        {
            var Q0;
            Q0=makeQuery(id+"F38.imprint","IMPRINT",FACE,{"disambiguationData":[TD([[makeQuery(id+"F38.imprint","IMPRINT",EDGE,{"derivedFrom":sQuery(id+"F38.wireOp",EDGE,"E82.bottom")}),1.0]])]});
            extrude(context, id + "F39", {"entities" : qUnion([Q0]), "operationType" : NewBodyOperationType.ADD, "depth" : 2.84 * mm, "offsetDistance" : 25.4 * mm});
        }
        {
            var Q0;
            Q0=makeQuery(id+"F39.opExtrude","SWEPT_EDGE",EDGE,{"disambiguationData":[OSD([sQuery(id+"F38.wireOp",EDGE,"E82.top"),sQuery(id+"F38.wireOp",EDGE,"E82.left")])]});
            var Q1;
            Q1=makeQuery(id+"F39.opExtrude","SWEPT_EDGE",EDGE,{"disambiguationData":[OSD([sQuery(id+"F38.wireOp",EDGE,"E82.top"),sQuery(id+"F38.wireOp",EDGE,"E82.right")])]});
            var Q2;
            Q2=makeQuery(id+"F39.opExtrude","SWEPT_EDGE",EDGE,{"disambiguationData":[OSD([sQuery(id+"F38.wireOp",EDGE,"E82.bottom"),sQuery(id+"F38.wireOp",EDGE,"E82.left")])]});
            var Q3;
            Q3=makeQuery(id+"F39.opExtrude","SWEPT_EDGE",EDGE,{"disambiguationData":[OSD([sQuery(id+"F38.wireOp",EDGE,"E82.bottom"),sQuery(id+"F38.wireOp",EDGE,"E82.right")])]});
            fillet(context, id + "F40", {"entities" : qUnion([Q0, Q1, Q2, Q3]), "radius" : 1.27 * mm, "tangentPropagation" : true, "allowEdgeOverflow" : false});
        }
        {
            var Q0;
            Q0=makeQuery(id+"F39.opExtrude","CAP_FACE",FACE,{"disambiguationData":[OSD([sQuery(id+"F38.wireOp",EDGE,"E82.bottom"),sQuery(id+"F38.wireOp",EDGE,"E82.top"),sQuery(id+"F38.wireOp",EDGE,"E82.left"),sQuery(id+"F38.wireOp",EDGE,"E82.right")])],"isStart":false});
            var sketch = newSketch(context, id + "F41", { "sketchPlane" : qUnion([Q0])});
            skLineSegment(sketch, "E83.bottom", {"start": v(-48.6, 37.12) * mm, "end": v(6.77, 37.12) * mm});
            skLineSegment(sketch, "E83.top", {"start": v(-48.6, -14.16) * mm, "end": v(6.77, -14.16) * mm});
            skLineSegment(sketch, "E83.left", {"start": v(-48.6, 37.12) * mm, "end": v(-48.6, -14.16) * mm});
            skLineSegment(sketch, "E83.right", {"start": v(6.77, 37.12) * mm, "end": v(6.77, -14.16) * mm});
            skSolve(sketch);
        }
        {
            var Q0;
            Q0=makeQuery(id+"F41.imprint","IMPRINT",FACE,{"disambiguationData":[TD([[makeQuery(id+"F41.imprint","IMPRINT",EDGE,{"derivedFrom":sQuery(id+"F41.wireOp",EDGE,"E83.bottom")}),-1.0]])]});
            extrude(context, id + "F42", {"entities" : qUnion([Q0]), "operationType" : NewBodyOperationType.REMOVE, "oppositeDirection" : true, "depth" : 5.7 * mm, "offsetDistance" : 25.4 * mm});
        }
        {
            var Q0;
            Q0=makeQuery(id+"F37.boolean.opBoolean","MERGE",FACE,{"derivedFrom":[makeQuery(id+"F36.boolean.opBoolean","MERGE",FACE,{"derivedFrom":[makeQuery(id+"F1.opExtrude","CAP_FACE",FACE,{"disambiguationData":[OSD([sQuery(id+"F0.wireOp",EDGE,"E0.bottom"),sQuery(id+"F0.wireOp",EDGE,"E0.top"),sQuery(id+"F0.wireOp",EDGE,"E0.left"),sQuery(id+"F0.wireOp",EDGE,"E0.right")])],"isStart":false}),makeQuery(id+"F36.opExtrude","SWEPT_FACE",FACE,{"disambiguationData":[OSD([sQuery(id+"F26.wireOp",EDGE,"E60.top"),sQuery(id+"F35.wireOp",EDGE,"E78")])]})]}),makeQuery(id+"F37.opExtrude","SWEPT_FACE",FACE,{"disambiguationData":[OSD([sQuery(id+"F21.wireOp",EDGE,"E56.top"),sQuery(id+"F34.wireOp",EDGE,"E70")])]})]});
            var sketch = newSketch(context, id + "F43", { "sketchPlane" : qUnion([Q0])});
            skLineSegment(sketch, "E84.bottom", {"start": v(-64.54, 38.98) * mm, "end": v(-153.44, 38.98) * mm});
            skLineSegment(sketch, "E84.top", {"start": v(-64.54, -40.4) * mm, "end": v(-100.58, -40.4) * mm});
            skLineSegment(sketch, "E84.left", {"start": v(-64.54, 38.98) * mm, "end": v(-64.54, -40.4) * mm});
            skLineSegment(sketch, "E84.right", {"start": v(-153.44, 38.98) * mm, "end": v(-153.44, -40.4) * mm});
            skLineSegment(sketch, "E85.top", {"start": v(-117.37, -31.61) * mm, "end": v(-100.58, -31.61) * mm});
            skLineSegment(sketch, "E85.left", {"start": v(-117.37, -40.4) * mm, "end": v(-117.37, -31.61) * mm});
            skLineSegment(sketch, "E85.right", {"start": v(-100.58, -40.4) * mm, "end": v(-100.58, -31.61) * mm});
            skLineSegment(sketch, "E86.trimOffspring", {"start": v(-117.37, -40.4) * mm, "end": v(-153.44, -40.4) * mm});
            skSolve(sketch);
        }
        {
            var Q0;
            Q0=makeQuery(id+"F43.imprint","IMPRINT",FACE,{"disambiguationData":[TD([[makeQuery(id+"F43.imprint","IMPRINT",EDGE,{"derivedFrom":sQuery(id+"F43.wireOp",EDGE,"E84.bottom")}),1.0]])]});
            extrude(context, id + "F44", {"entities" : qUnion([Q0]), "operationType" : NewBodyOperationType.ADD, "depth" : 2.84 * mm, "offsetDistance" : 25.4 * mm});
        }
        {
            var Q0;
            Q0=makeQuery(id+"F44.opExtrude","SWEPT_EDGE",EDGE,{"disambiguationData":[OSD([sQuery(id+"F43.wireOp",EDGE,"E84.top"),sQuery(id+"F43.wireOp",EDGE,"E84.left")])]});
            var Q1;
            Q1=makeQuery(id+"F44.opExtrude","SWEPT_EDGE",EDGE,{"disambiguationData":[OSD([sQuery(id+"F43.wireOp",EDGE,"E84.top"),sQuery(id+"F43.wireOp",EDGE,"E85.right")])]});
            var Q2;
            Q2=makeQuery(id+"F44.opExtrude","SWEPT_EDGE",EDGE,{"disambiguationData":[OSD([sQuery(id+"F43.wireOp",EDGE,"E85.top"),sQuery(id+"F43.wireOp",EDGE,"E85.right")])]});
            var Q3;
            Q3=makeQuery(id+"F44.opExtrude","SWEPT_EDGE",EDGE,{"disambiguationData":[OSD([sQuery(id+"F43.wireOp",EDGE,"E85.top"),sQuery(id+"F43.wireOp",EDGE,"E85.left")])]});
            var Q4;
            Q4=makeQuery(id+"F44.opExtrude","SWEPT_EDGE",EDGE,{"disambiguationData":[OSD([sQuery(id+"F43.wireOp",EDGE,"E85.left"),sQuery(id+"F43.wireOp",EDGE,"E86.trimOffspring")])]});
            var Q5;
            Q5=makeQuery(id+"F44.opExtrude","SWEPT_EDGE",EDGE,{"disambiguationData":[OSD([sQuery(id+"F43.wireOp",EDGE,"E84.right"),sQuery(id+"F43.wireOp",EDGE,"E86.trimOffspring")])]});
            var Q6;
            Q6=makeQuery(id+"F44.opExtrude","SWEPT_EDGE",EDGE,{"disambiguationData":[OSD([sQuery(id+"F43.wireOp",EDGE,"E84.bottom"),sQuery(id+"F43.wireOp",EDGE,"E84.left")])]});
            var Q7;
            Q7=makeQuery(id+"F44.opExtrude","SWEPT_EDGE",EDGE,{"disambiguationData":[OSD([sQuery(id+"F43.wireOp",EDGE,"E84.bottom"),sQuery(id+"F43.wireOp",EDGE,"E84.right")])]});
            fillet(context, id + "F45", {"entities" : qUnion([Q0, Q1, Q2, Q3, Q4, Q5, Q6, Q7]), "radius" : 1.27 * mm, "tangentPropagation" : true, "allowEdgeOverflow" : false});
        }
        {
            var Q0;
            Q0=makeQuery(id+"F44.opExtrude","CAP_FACE",FACE,{"disambiguationData":[OSD([sQuery(id+"F43.wireOp",EDGE,"E84.bottom"),sQuery(id+"F43.wireOp",EDGE,"E84.top"),sQuery(id+"F43.wireOp",EDGE,"E84.left"),sQuery(id+"F43.wireOp",EDGE,"E84.right"),sQuery(id+"F43.wireOp",EDGE,"E85.top"),sQuery(id+"F43.wireOp",EDGE,"E85.left"),sQuery(id+"F43.wireOp",EDGE,"E85.right"),sQuery(id+"F43.wireOp",EDGE,"E86.trimOffspring")])],"isStart":false});
            var sketch = newSketch(context, id + "F46", { "sketchPlane" : qUnion([Q0])});
            skArc(sketch, "E87.0", {"start": v(-101.85, -29.76) * mm, "mid": v(-99.64, -30.67) * mm, "end": v(-98.73, -32.88) * mm});
            skLineSegment(sketch, "E87.1", {"start": v(-116.1, -29.76) * mm, "end": v(-101.85, -29.76) * mm});
            skLineSegment(sketch, "E87.2", {"start": v(-98.73, -32.88) * mm, "end": v(-98.73, -38.54) * mm});
            skArc(sketch, "E87.3", {"start": v(-119.23, -32.88) * mm, "mid": v(-118.31, -30.67) * mm, "end": v(-116.1, -29.76) * mm});
            skLineSegment(sketch, "E87.4", {"start": v(-119.23, -38.54) * mm, "end": v(-119.23, -32.88) * mm});
            skLineSegment(sketch, "E87.5", {"start": v(-151.59, -38.54) * mm, "end": v(-119.23, -38.54) * mm});
            skLineSegment(sketch, "E87.6", {"start": v(-98.73, -38.54) * mm, "end": v(-66.4, -38.54) * mm});
            skLineSegment(sketch, "E87.7", {"start": v(-66.4, -38.54) * mm, "end": v(-66.4, 37.12) * mm});
            skLineSegment(sketch, "E87.8", {"start": v(-66.4, 37.12) * mm, "end": v(-151.59, 37.12) * mm});
            skLineSegment(sketch, "E87.9", {"start": v(-151.59, 37.12) * mm, "end": v(-151.59, -38.54) * mm});
            skSolve(sketch);
        }
        {
            var Q0;
            Q0=makeQuery(id+"F46.imprint","IMPRINT",FACE,{"disambiguationData":[TD([[makeQuery(id+"F46.imprint","IMPRINT",EDGE,{"derivedFrom":sQuery(id+"F46.wireOp",EDGE,"E87.0")}),1.0]])]});
            extrude(context, id + "F47", {"entities" : qUnion([Q0]), "operationType" : NewBodyOperationType.REMOVE, "oppositeDirection" : true, "depth" : 5.7 * mm, "offsetDistance" : 25.4 * mm});
        }
        {
            var Q0;
            Q0=makeQuery(id+"F37.boolean.opBoolean","MERGE",FACE,{"derivedFrom":[makeQuery(id+"F36.boolean.opBoolean","MERGE",FACE,{"derivedFrom":[makeQuery(id+"F1.opExtrude","CAP_FACE",FACE,{"disambiguationData":[OSD([sQuery(id+"F0.wireOp",EDGE,"E0.bottom"),sQuery(id+"F0.wireOp",EDGE,"E0.top"),sQuery(id+"F0.wireOp",EDGE,"E0.left"),sQuery(id+"F0.wireOp",EDGE,"E0.right")])],"isStart":false}),makeQuery(id+"F36.opExtrude","SWEPT_FACE",FACE,{"disambiguationData":[OSD([sQuery(id+"F26.wireOp",EDGE,"E60.top"),sQuery(id+"F35.wireOp",EDGE,"E78")])]})]}),makeQuery(id+"F37.opExtrude","SWEPT_FACE",FACE,{"disambiguationData":[OSD([sQuery(id+"F21.wireOp",EDGE,"E56.top"),sQuery(id+"F34.wireOp",EDGE,"E70")])]})]});
            var sketch = newSketch(context, id + "F48", { "sketchPlane" : qUnion([Q0])});
            skLineSegment(sketch, "E88", {"start": v(63.1, 3.67) * mm, "end": v(52.18, -9.03) * mm});
            skPoint(sketch, "E88.endSnap0", {"position": v(52.18, 3.67) * mm});
            skLineSegment(sketch, "E89", {"start": v(52.18, -9.03) * mm, "end": v(41.26, 3.67) * mm});
            skLineSegment(sketch, "E90", {"start": v(41.26, 3.67) * mm, "end": v(63.1, 3.67) * mm});
            skLineSegment(sketch, "E91", {"start": v(136.33, 3.68) * mm, "end": v(125.4, -9.02) * mm});
            skLineSegment(sketch, "E92", {"start": v(125.4, -9.02) * mm, "end": v(114.48, 3.68) * mm});
            skSolve(sketch);
        }
        {
            var Q0;
            Q0=makeQuery(id+"F48.imprint","IMPRINT",FACE,{"disambiguationData":[TD([[makeQuery(id+"F48.imprint","IMPRINT",EDGE,{"derivedFrom":sQuery(id+"F48.wireOp",EDGE,"E88")}),-1.0]])]});
            var Q1;
            {var subQ0=sQuery(id+"F48.wireOp",EDGE,"E91");Q1=makeQuery(id+"F48.imprint","IMPRINT",FACE,{"disambiguationData":[TD([[makeQuery(id+"F48.imprint","IMPRINT",EDGE,{"derivedFrom":subQ0}),-1.0]])]});}
            extrude(context, id + "F49", {"entities" : qUnion([Q0, Q1]), "operationType" : NewBodyOperationType.REMOVE, "oppositeDirection" : true, "depth" : 0.4 * mm, "offsetDistance" : 25.4 * mm});
        }
        {
            var Q0;
            Q0=makeQuery(id+"F49.boolean.opBoolean","COPY",EDGE,{"derivedFrom":makeQuery(id+"F49.opExtrude","SWEPT_EDGE",EDGE,{"disambiguationData":[OSD([sQuery(id+"F48.wireOp",EDGE,"E91"),sQuery(id+"F48.wireOp",EDGE,"E92")])]})});
            var Q1;
            Q1=makeQuery(id+"F49.boolean.opBoolean","COPY",EDGE,{"derivedFrom":makeQuery(id+"F49.opExtrude","SWEPT_EDGE",EDGE,{"disambiguationData":[OSD([sQuery(id+"F48.wireOp",EDGE,"E88"),sQuery(id+"F48.wireOp",EDGE,"E89")])]})});
            fillet(context, id + "F50", {"entities" : qUnion([Q0, Q1]), "radius" : 6.35 * mm, "tangentPropagation" : true, "allowEdgeOverflow" : false});
        }
        {
            var Q0;
            Q0=makeQuery(id+"F37.boolean.opBoolean","MERGE",FACE,{"derivedFrom":[makeQuery(id+"F36.boolean.opBoolean","MERGE",FACE,{"derivedFrom":[makeQuery(id+"F1.opExtrude","CAP_FACE",FACE,{"disambiguationData":[OSD([sQuery(id+"F0.wireOp",EDGE,"E0.bottom"),sQuery(id+"F0.wireOp",EDGE,"E0.top"),sQuery(id+"F0.wireOp",EDGE,"E0.left"),sQuery(id+"F0.wireOp",EDGE,"E0.right")])],"isStart":false}),makeQuery(id+"F36.opExtrude","SWEPT_FACE",FACE,{"disambiguationData":[OSD([sQuery(id+"F26.wireOp",EDGE,"E60.top"),sQuery(id+"F35.wireOp",EDGE,"E78")])]})]}),makeQuery(id+"F37.opExtrude","SWEPT_FACE",FACE,{"disambiguationData":[OSD([sQuery(id+"F21.wireOp",EDGE,"E56.top"),sQuery(id+"F34.wireOp",EDGE,"E70")])]})]});
            var sketch = newSketch(context, id + "F51", { "sketchPlane" : qUnion([Q0])});
            skCircle(sketch, "E93", {"center": v(-57.4, 34.24) * mm, "radius": 4.76 * mm});
            skCircle(sketch, "E94", {"center": v(-57.4, -7.04) * mm, "radius": 4.76 * mm});
            skCircle(sketch, "E95", {"center": v(15.77, -7.05) * mm, "radius": 4.76 * mm});
            skCircle(sketch, "E96", {"center": v(15.77, 34.23) * mm, "radius": 4.76 * mm});
            skCircle(sketch, "E97", {"center": v(88.8, 34.24) * mm, "radius": 4.76 * mm});
            skCircle(sketch, "E98", {"center": v(88.8, -7.04) * mm, "radius": 4.76 * mm});
            skCircle(sketch, "E99", {"center": v(147.71, -7.13) * mm, "radius": 4.76 * mm});
            skLineSegment(sketch, "E100", {"start": v(16.63, -2.36) * mm, "end": v(152.77, -2.36) * mm, "construction": true});
            skSolve(sketch);
        }
        {
            var Q0;
            Q0=makeQuery(id+"F51.imprint","IMPRINT",FACE,{"disambiguationData":[TD([[makeQuery(id+"F51.imprint","IMPRINT",EDGE,{"derivedFrom":sQuery(id+"F51.wireOp",EDGE,"E93")}),1.0]])]});
            var Q1;
            Q1=makeQuery(id+"F51.imprint","IMPRINT",FACE,{"disambiguationData":[TD([[makeQuery(id+"F51.imprint","IMPRINT",EDGE,{"derivedFrom":sQuery(id+"F51.wireOp",EDGE,"E94")}),1.0]])]});
            var Q2;
            Q2=makeQuery(id+"F51.imprint","IMPRINT",FACE,{"disambiguationData":[TD([[makeQuery(id+"F51.imprint","IMPRINT",EDGE,{"derivedFrom":sQuery(id+"F51.wireOp",EDGE,"E96")}),1.0]])]});
            var Q3;
            Q3=makeQuery(id+"F51.imprint","IMPRINT",FACE,{"disambiguationData":[TD([[makeQuery(id+"F51.imprint","IMPRINT",EDGE,{"derivedFrom":sQuery(id+"F51.wireOp",EDGE,"E95")}),1.0]])]});
            var Q4;
            Q4=makeQuery(id+"F51.imprint","IMPRINT",FACE,{"disambiguationData":[TD([[makeQuery(id+"F51.imprint","IMPRINT",EDGE,{"derivedFrom":sQuery(id+"F51.wireOp",EDGE,"E98")}),1.0]])]});
            var Q5;
            Q5=makeQuery(id+"F51.imprint","IMPRINT",FACE,{"disambiguationData":[TD([[makeQuery(id+"F51.imprint","IMPRINT",EDGE,{"derivedFrom":sQuery(id+"F51.wireOp",EDGE,"E97")}),1.0]])]});
            var Q6;
            Q6=makeQuery(id+"F51.imprint","IMPRINT",FACE,{"disambiguationData":[TD([[makeQuery(id+"F51.imprint","IMPRINT",EDGE,{"derivedFrom":sQuery(id+"F51.wireOp",EDGE,"E99")}),1.0]])]});
            extrude(context, id + "F52", {"entities" : qUnion([Q0, Q1, Q2, Q3, Q4, Q5, Q6]), "operationType" : NewBodyOperationType.REMOVE, "oppositeDirection" : true, "depth" : 0.4 * mm, "offsetDistance" : 25.4 * mm});
        }
        {
            var Q0;
            Q0=makeQuery(id+"F37.boolean.opBoolean","MERGE",FACE,{"derivedFrom":[makeQuery(id+"F36.boolean.opBoolean","MERGE",FACE,{"derivedFrom":[makeQuery(id+"F1.opExtrude","CAP_FACE",FACE,{"disambiguationData":[OSD([sQuery(id+"F0.wireOp",EDGE,"E0.bottom"),sQuery(id+"F0.wireOp",EDGE,"E0.top"),sQuery(id+"F0.wireOp",EDGE,"E0.left"),sQuery(id+"F0.wireOp",EDGE,"E0.right")])],"isStart":false}),makeQuery(id+"F36.opExtrude","SWEPT_FACE",FACE,{"disambiguationData":[OSD([sQuery(id+"F26.wireOp",EDGE,"E60.top"),sQuery(id+"F35.wireOp",EDGE,"E78")])]})]}),makeQuery(id+"F37.opExtrude","SWEPT_FACE",FACE,{"disambiguationData":[OSD([sQuery(id+"F21.wireOp",EDGE,"E56.top"),sQuery(id+"F34.wireOp",EDGE,"E70")])]})]});
            var sketch = newSketch(context, id + "F53", { "sketchPlane" : qUnion([Q0])});
            skCircle(sketch, "E101", {"center": v(-108.98, -37.17) * mm, "radius": 2.39 * mm});
            skPoint(sketch, "E101.centerSnap0", {"position": v(-108.98, -31.61) * mm});
            skSolve(sketch);
        }
        {
            var Q0;
            Q0=makeQuery(id+"F53.imprint","IMPRINT",FACE,{"disambiguationData":[TD([[makeQuery(id+"F53.imprint","IMPRINT",EDGE,{"derivedFrom":sQuery(id+"F53.wireOp",EDGE,"E101")}),1.0]])]});
            extrude(context, id + "F54", {"entities" : qUnion([Q0]), "operationType" : NewBodyOperationType.REMOVE, "oppositeDirection" : true, "depth" : 2.54 * mm, "offsetDistance" : 25.4 * mm});
        }
        {
            var Q0;
            Q0=makeQuery(id+"F37.boolean.opBoolean","MERGE",FACE,{"derivedFrom":[makeQuery(id+"F36.boolean.opBoolean","MERGE",FACE,{"derivedFrom":[makeQuery(id+"F1.opExtrude","CAP_FACE",FACE,{"disambiguationData":[OSD([sQuery(id+"F0.wireOp",EDGE,"E0.bottom"),sQuery(id+"F0.wireOp",EDGE,"E0.top"),sQuery(id+"F0.wireOp",EDGE,"E0.left"),sQuery(id+"F0.wireOp",EDGE,"E0.right")])],"isStart":false}),makeQuery(id+"F36.opExtrude","SWEPT_FACE",FACE,{"disambiguationData":[OSD([sQuery(id+"F26.wireOp",EDGE,"E60.top"),sQuery(id+"F35.wireOp",EDGE,"E78")])]})]}),makeQuery(id+"F37.opExtrude","SWEPT_FACE",FACE,{"disambiguationData":[OSD([sQuery(id+"F21.wireOp",EDGE,"E56.top"),sQuery(id+"F34.wireOp",EDGE,"E70")])]})]});
            var sketch = newSketch(context, id + "F55", { "sketchPlane" : qUnion([Q0])});
            skLineSegment(sketch, "E102.bottom", {"start": v(-29.34, -24.7) * mm, "end": v(138.93, -24.7) * mm});
            skLineSegment(sketch, "E102.top", {"start": v(-29.34, -40.58) * mm, "end": v(138.93, -40.58) * mm});
            skLineSegment(sketch, "E103", {"start": v(-29.34, -40.58) * mm, "end": v(-42.04, -32.64) * mm});
            skPoint(sketch, "E103.endSnap0", {"position": v(-29.34, -32.64) * mm});
            skLineSegment(sketch, "E104", {"start": v(-42.04, -32.64) * mm, "end": v(-29.34, -24.7) * mm});
            skLineSegment(sketch, "E105", {"start": v(138.93, -40.58) * mm, "end": v(151.63, -32.64) * mm});
            skPoint(sketch, "E105.endSnap0", {"position": v(138.93, -32.64) * mm});
            skLineSegment(sketch, "E106", {"start": v(151.63, -32.64) * mm, "end": v(138.93, -24.7) * mm});
            skSolve(sketch);
        }
        {
            var Q0;
            Q0=makeQuery(id+"F55.imprint","IMPRINT",FACE,{"disambiguationData":[TD([[makeQuery(id+"F55.imprint","IMPRINT",EDGE,{"derivedFrom":sQuery(id+"F55.wireOp",EDGE,"E102.bottom")}),-1.0]])]});
            extrude(context, id + "F56", {"entities" : qUnion([Q0]), "operationType" : NewBodyOperationType.ADD, "depth" : 2.84 * mm, "offsetDistance" : 25.4 * mm});
        }
        {
            var Q0;
            Q0=makeQuery(id+"F56.opExtrude","SWEPT_EDGE",EDGE,{"disambiguationData":[OSD([sQuery(id+"F55.wireOp",EDGE,"E103"),sQuery(id+"F55.wireOp",EDGE,"E104")])]});
            var Q1;
            Q1=makeQuery(id+"F56.opExtrude","SWEPT_EDGE",EDGE,{"disambiguationData":[OSD([sQuery(id+"F55.wireOp",EDGE,"E102.top"),sQuery(id+"F55.wireOp",EDGE,"E103")])]});
            var Q2;
            Q2=makeQuery(id+"F56.opExtrude","SWEPT_EDGE",EDGE,{"disambiguationData":[OSD([sQuery(id+"F55.wireOp",EDGE,"E102.bottom"),sQuery(id+"F55.wireOp",EDGE,"E104")])]});
            var Q3;
            Q3=makeQuery(id+"F56.opExtrude","SWEPT_EDGE",EDGE,{"disambiguationData":[OSD([sQuery(id+"F55.wireOp",EDGE,"E105"),sQuery(id+"F55.wireOp",EDGE,"E106")])]});
            var Q4;
            Q4=makeQuery(id+"F56.opExtrude","SWEPT_EDGE",EDGE,{"disambiguationData":[OSD([sQuery(id+"F55.wireOp",EDGE,"E102.top"),sQuery(id+"F55.wireOp",EDGE,"E105")])]});
            var Q5;
            Q5=makeQuery(id+"F56.opExtrude","SWEPT_EDGE",EDGE,{"disambiguationData":[OSD([sQuery(id+"F55.wireOp",EDGE,"E102.bottom"),sQuery(id+"F55.wireOp",EDGE,"E106")])]});
            fillet(context, id + "F57", {"entities" : qUnion([Q0, Q1, Q2, Q3, Q4, Q5]), "radius" : 1.27 * mm, "tangentPropagation" : true, "allowEdgeOverflow" : false});
        }
        {
            var Q0;
            Q0=makeQuery(id+"F56.opExtrude","CAP_FACE",FACE,{"disambiguationData":[OSD([sQuery(id+"F55.wireOp",EDGE,"E102.bottom"),sQuery(id+"F55.wireOp",EDGE,"E102.top"),sQuery(id+"F55.wireOp",EDGE,"E103"),sQuery(id+"F55.wireOp",EDGE,"E104"),sQuery(id+"F55.wireOp",EDGE,"E105"),sQuery(id+"F55.wireOp",EDGE,"E106")])],"isStart":false});
            var sketch = newSketch(context, id + "F58", { "sketchPlane" : qUnion([Q0])});
            skLineSegment(sketch, "E107", {"start": v(54.8, -24.7) * mm, "end": v(54.8, -40.58) * mm, "construction": true});
            skLineSegment(sketch, "E108.bottom", {"start": v(67.5, -26.56) * mm, "end": v(42.1, -26.56) * mm});
            skLineSegment(sketch, "E108.top", {"start": v(67.5, -38.72) * mm, "end": v(42.1, -38.72) * mm});
            skLineSegment(sketch, "E108.left", {"start": v(67.5, -26.56) * mm, "end": v(67.5, -38.72) * mm});
            skLineSegment(sketch, "E108.right", {"start": v(42.1, -26.56) * mm, "end": v(42.1, -38.72) * mm});
            skPoint(sketch, "E108.middle", {"position": v(54.8, -32.64) * mm});
            skLineSegment(sketch, "E109.bottom", {"start": v(69.35, -26.56) * mm, "end": v(136.56, -26.56) * mm});
            skLineSegment(sketch, "E109.top", {"start": v(69.35, -38.72) * mm, "end": v(136.56, -38.72) * mm});
            skLineSegment(sketch, "E109.left", {"start": v(69.35, -26.56) * mm, "end": v(69.35, -38.72) * mm});
            skLineSegment(sketch, "E109.right", {"start": v(136.56, -26.56) * mm, "end": v(136.56, -38.72) * mm});
            skLineSegment(sketch, "E110.bottom", {"start": v(40.24, -26.56) * mm, "end": v(-27.12, -26.56) * mm});
            skLineSegment(sketch, "E110.top", {"start": v(40.24, -38.72) * mm, "end": v(-27.12, -38.72) * mm});
            skLineSegment(sketch, "E110.left", {"start": v(40.24, -26.56) * mm, "end": v(40.24, -38.72) * mm});
            skLineSegment(sketch, "E110.right", {"start": v(-27.12, -26.56) * mm, "end": v(-27.12, -38.72) * mm});
            skLineSegment(sketch, "E111", {"start": v(138.42, -38.72) * mm, "end": v(138.42, -26.56) * mm});
            skLineSegment(sketch, "E112", {"start": v(138.42, -26.56) * mm, "end": v(148.12, -32.64) * mm});
            skPoint(sketch, "E112.endSnap0", {"position": v(138.42, -32.64) * mm});
            skLineSegment(sketch, "E113", {"start": v(148.12, -32.64) * mm, "end": v(138.42, -38.72) * mm});
            skLineSegment(sketch, "E114", {"start": v(-28.98, -38.72) * mm, "end": v(-28.98, -26.56) * mm});
            skLineSegment(sketch, "E115", {"start": v(-28.98, -26.56) * mm, "end": v(-38.4, -32.64) * mm});
            skPoint(sketch, "E115.endSnap0", {"position": v(-27.12, -32.64) * mm});
            skLineSegment(sketch, "E116", {"start": v(-38.4, -32.64) * mm, "end": v(-28.98, -38.72) * mm});
            skSolve(sketch);
        }
        {
            var Q0;
            Q0=makeQuery(id+"F58.imprint","IMPRINT",FACE,{"disambiguationData":[TD([[makeQuery(id+"F58.imprint","IMPRINT",EDGE,{"derivedFrom":sQuery(id+"F58.wireOp",EDGE,"E114")}),1.0]])]});
            var Q1;
            Q1=makeQuery(id+"F58.imprint","IMPRINT",FACE,{"disambiguationData":[TD([[makeQuery(id+"F58.imprint","IMPRINT",EDGE,{"derivedFrom":sQuery(id+"F58.wireOp",EDGE,"E110.bottom")}),1.0]])]});
            var Q2;
            Q2=makeQuery(id+"F58.imprint","IMPRINT",FACE,{"disambiguationData":[TD([[makeQuery(id+"F58.imprint","IMPRINT",EDGE,{"derivedFrom":sQuery(id+"F58.wireOp",EDGE,"E108.bottom")}),1.0]])]});
            var Q3;
            Q3=makeQuery(id+"F58.imprint","IMPRINT",FACE,{"disambiguationData":[TD([[makeQuery(id+"F58.imprint","IMPRINT",EDGE,{"derivedFrom":sQuery(id+"F58.wireOp",EDGE,"E109.bottom")}),-1.0]])]});
            var Q4;
            Q4=makeQuery(id+"F58.imprint","IMPRINT",FACE,{"disambiguationData":[TD([[makeQuery(id+"F58.imprint","IMPRINT",EDGE,{"derivedFrom":sQuery(id+"F58.wireOp",EDGE,"E111")}),-1.0]])]});
            extrude(context, id + "F59", {"entities" : qUnion([Q0, Q1, Q2, Q3, Q4]), "operationType" : NewBodyOperationType.REMOVE, "oppositeDirection" : true, "depth" : 5.7 * mm, "offsetDistance" : 25.4 * mm});
        }
        {
            var Q0;
            Q0=makeQuery(id+"F59.boolean.opBoolean","COPY",EDGE,{"derivedFrom":makeQuery(id+"F59.opExtrude","SWEPT_EDGE",EDGE,{"disambiguationData":[OSD([sQuery(id+"F58.wireOp",EDGE,"E115"),sQuery(id+"F58.wireOp",EDGE,"E116")])]})});
            var Q1;
            Q1=makeQuery(id+"F59.boolean.opBoolean","COPY",EDGE,{"derivedFrom":makeQuery(id+"F59.opExtrude","SWEPT_EDGE",EDGE,{"disambiguationData":[OSD([sQuery(id+"F58.wireOp",EDGE,"E114"),sQuery(id+"F58.wireOp",EDGE,"E116")])]})});
            var Q2;
            Q2=makeQuery(id+"F59.boolean.opBoolean","COPY",EDGE,{"derivedFrom":makeQuery(id+"F59.opExtrude","SWEPT_EDGE",EDGE,{"disambiguationData":[OSD([sQuery(id+"F58.wireOp",EDGE,"E114"),sQuery(id+"F58.wireOp",EDGE,"E115")])]})});
            var Q3;
            Q3=makeQuery(id+"F59.boolean.opBoolean","COPY",EDGE,{"derivedFrom":makeQuery(id+"F59.opExtrude","SWEPT_EDGE",EDGE,{"disambiguationData":[OSD([sQuery(id+"F58.wireOp",EDGE,"E110.bottom"),sQuery(id+"F58.wireOp",EDGE,"E110.right")])]})});
            var Q4;
            Q4=makeQuery(id+"F59.boolean.opBoolean","COPY",EDGE,{"derivedFrom":makeQuery(id+"F59.opExtrude","SWEPT_EDGE",EDGE,{"disambiguationData":[OSD([sQuery(id+"F58.wireOp",EDGE,"E110.top"),sQuery(id+"F58.wireOp",EDGE,"E110.right")])]})});
            var Q5;
            Q5=makeQuery(id+"F59.boolean.opBoolean","COPY",EDGE,{"derivedFrom":makeQuery(id+"F59.opExtrude","SWEPT_EDGE",EDGE,{"disambiguationData":[OSD([sQuery(id+"F58.wireOp",EDGE,"E109.top"),sQuery(id+"F58.wireOp",EDGE,"E109.left")])]})});
            var Q6;
            Q6=makeQuery(id+"F59.boolean.opBoolean","COPY",EDGE,{"derivedFrom":makeQuery(id+"F59.opExtrude","SWEPT_EDGE",EDGE,{"disambiguationData":[OSD([sQuery(id+"F58.wireOp",EDGE,"E108.top"),sQuery(id+"F58.wireOp",EDGE,"E108.right")])]})});
            var Q7;
            Q7=makeQuery(id+"F59.boolean.opBoolean","COPY",EDGE,{"derivedFrom":makeQuery(id+"F59.opExtrude","SWEPT_EDGE",EDGE,{"disambiguationData":[OSD([sQuery(id+"F58.wireOp",EDGE,"E108.bottom"),sQuery(id+"F58.wireOp",EDGE,"E108.right")])]})});
            var Q8;
            Q8=makeQuery(id+"F59.boolean.opBoolean","COPY",EDGE,{"derivedFrom":makeQuery(id+"F59.opExtrude","SWEPT_EDGE",EDGE,{"disambiguationData":[OSD([sQuery(id+"F58.wireOp",EDGE,"E109.bottom"),sQuery(id+"F58.wireOp",EDGE,"E109.left")])]})});
            var Q9;
            Q9=makeQuery(id+"F59.boolean.opBoolean","COPY",EDGE,{"derivedFrom":makeQuery(id+"F59.opExtrude","SWEPT_EDGE",EDGE,{"disambiguationData":[OSD([sQuery(id+"F58.wireOp",EDGE,"E108.bottom"),sQuery(id+"F58.wireOp",EDGE,"E108.left")])]})});
            var Q10;
            Q10=makeQuery(id+"F59.boolean.opBoolean","COPY",EDGE,{"derivedFrom":makeQuery(id+"F59.opExtrude","SWEPT_EDGE",EDGE,{"disambiguationData":[OSD([sQuery(id+"F58.wireOp",EDGE,"E110.bottom"),sQuery(id+"F58.wireOp",EDGE,"E110.left")])]})});
            var Q11;
            Q11=makeQuery(id+"F59.boolean.opBoolean","COPY",EDGE,{"derivedFrom":makeQuery(id+"F59.opExtrude","SWEPT_EDGE",EDGE,{"disambiguationData":[OSD([sQuery(id+"F58.wireOp",EDGE,"E110.top"),sQuery(id+"F58.wireOp",EDGE,"E110.left")])]})});
            var Q12;
            Q12=makeQuery(id+"F59.boolean.opBoolean","COPY",EDGE,{"derivedFrom":makeQuery(id+"F59.opExtrude","SWEPT_EDGE",EDGE,{"disambiguationData":[OSD([sQuery(id+"F58.wireOp",EDGE,"E108.top"),sQuery(id+"F58.wireOp",EDGE,"E108.left")])]})});
            var Q13;
            Q13=makeQuery(id+"F59.boolean.opBoolean","COPY",EDGE,{"derivedFrom":makeQuery(id+"F59.opExtrude","SWEPT_EDGE",EDGE,{"disambiguationData":[OSD([sQuery(id+"F58.wireOp",EDGE,"E109.top"),sQuery(id+"F58.wireOp",EDGE,"E109.right")])]})});
            var Q14;
            Q14=makeQuery(id+"F59.boolean.opBoolean","COPY",EDGE,{"derivedFrom":makeQuery(id+"F59.opExtrude","SWEPT_EDGE",EDGE,{"disambiguationData":[OSD([sQuery(id+"F58.wireOp",EDGE,"E109.bottom"),sQuery(id+"F58.wireOp",EDGE,"E109.right")])]})});
            var Q15;
            Q15=makeQuery(id+"F59.boolean.opBoolean","COPY",EDGE,{"derivedFrom":makeQuery(id+"F59.opExtrude","SWEPT_EDGE",EDGE,{"disambiguationData":[OSD([sQuery(id+"F58.wireOp",EDGE,"E112"),sQuery(id+"F58.wireOp",EDGE,"E113")])]})});
            var Q16;
            Q16=makeQuery(id+"F59.boolean.opBoolean","COPY",EDGE,{"derivedFrom":makeQuery(id+"F59.opExtrude","SWEPT_EDGE",EDGE,{"disambiguationData":[OSD([sQuery(id+"F58.wireOp",EDGE,"E111"),sQuery(id+"F58.wireOp",EDGE,"E112")])]})});
            var Q17;
            Q17=makeQuery(id+"F59.boolean.opBoolean","COPY",EDGE,{"derivedFrom":makeQuery(id+"F59.opExtrude","SWEPT_EDGE",EDGE,{"disambiguationData":[OSD([sQuery(id+"F58.wireOp",EDGE,"E111"),sQuery(id+"F58.wireOp",EDGE,"E113")])]})});
            fillet(context, id + "F60", {"entities" : qUnion([Q0, Q1, Q2, Q3, Q4, Q5, Q6, Q7, Q8, Q9, Q10, Q11, Q12, Q13, Q14, Q15, Q16, Q17]), "radius" : 0.25 * mm, "tangentPropagation" : true, "allowEdgeOverflow" : false});
        }
        {
            var Q0;
            Q0=makeQuery(id+"F37.boolean.opBoolean","MERGE",FACE,{"derivedFrom":[makeQuery(id+"F36.boolean.opBoolean","MERGE",FACE,{"derivedFrom":[makeQuery(id+"F1.opExtrude","CAP_FACE",FACE,{"disambiguationData":[OSD([sQuery(id+"F0.wireOp",EDGE,"E0.bottom"),sQuery(id+"F0.wireOp",EDGE,"E0.top"),sQuery(id+"F0.wireOp",EDGE,"E0.left"),sQuery(id+"F0.wireOp",EDGE,"E0.right")])],"isStart":false}),makeQuery(id+"F36.opExtrude","SWEPT_FACE",FACE,{"disambiguationData":[OSD([sQuery(id+"F26.wireOp",EDGE,"E60.top"),sQuery(id+"F35.wireOp",EDGE,"E78")])]})]}),makeQuery(id+"F37.opExtrude","SWEPT_FACE",FACE,{"disambiguationData":[OSD([sQuery(id+"F21.wireOp",EDGE,"E56.top"),sQuery(id+"F34.wireOp",EDGE,"E70")])]})]});
            var sketch = newSketch(context, id + "F61", { "sketchPlane" : qUnion([Q0])});
            skCircle(sketch, "E117", {"center": v(-57.47, -40.58) * mm, "radius": 3.18 * mm});
            skCircle(sketch, "E118", {"center": v(23.9, -43.74) * mm, "radius": 1.59 * mm});
            skCircle(sketch, "E119", {"center": v(39.23, -43.74) * mm, "radius": 1.59 * mm});
            skCircle(sketch, "E120", {"center": v(86.86, -43.74) * mm, "radius": 1.59 * mm});
            skCircle(sketch, "E121", {"center": v(147.88, -38.74) * mm, "radius": 1.59 * mm});
            skCircle(sketch, "E122", {"center": v(-10.07, 43.74) * mm, "radius": 1.59 * mm});
            skCircle(sketch, "E123", {"center": v(5.5, 43.74) * mm, "radius": 1.59 * mm});
            skCircle(sketch, "E124", {"center": v(63.08, 43.74) * mm, "radius": 1.59 * mm});
            skCircle(sketch, "E125", {"center": v(-109, 43.74) * mm, "radius": 1.59 * mm});
            skPoint(sketch, "E125.centerSnap0", {"position": v(-109, 38.98) * mm});
            skSolve(sketch);
        }
        {
            var Q0;
            Q0=makeQuery(id+"F61.imprint","IMPRINT",FACE,{"disambiguationData":[TD([[makeQuery(id+"F61.imprint","IMPRINT",EDGE,{"derivedFrom":sQuery(id+"F61.wireOp",EDGE,"E125")}),1.0]])]});
            var Q1;
            Q1=makeQuery(id+"F61.imprint","IMPRINT",FACE,{"disambiguationData":[TD([[makeQuery(id+"F61.imprint","IMPRINT",EDGE,{"derivedFrom":sQuery(id+"F61.wireOp",EDGE,"E122")}),1.0]])]});
            var Q2;
            Q2=makeQuery(id+"F61.imprint","IMPRINT",FACE,{"disambiguationData":[TD([[makeQuery(id+"F61.imprint","IMPRINT",EDGE,{"derivedFrom":sQuery(id+"F61.wireOp",EDGE,"E123")}),1.0]])]});
            var Q3;
            Q3=makeQuery(id+"F61.imprint","IMPRINT",FACE,{"disambiguationData":[TD([[makeQuery(id+"F61.imprint","IMPRINT",EDGE,{"derivedFrom":sQuery(id+"F61.wireOp",EDGE,"E117")}),1.0]])]});
            var Q4;
            Q4=makeQuery(id+"F61.imprint","IMPRINT",FACE,{"disambiguationData":[TD([[makeQuery(id+"F61.imprint","IMPRINT",EDGE,{"derivedFrom":sQuery(id+"F61.wireOp",EDGE,"E118")}),1.0]])]});
            var Q5;
            Q5=makeQuery(id+"F61.imprint","IMPRINT",FACE,{"disambiguationData":[TD([[makeQuery(id+"F61.imprint","IMPRINT",EDGE,{"derivedFrom":sQuery(id+"F61.wireOp",EDGE,"E119")}),1.0]])]});
            var Q6;
            Q6=makeQuery(id+"F61.imprint","IMPRINT",FACE,{"disambiguationData":[TD([[makeQuery(id+"F61.imprint","IMPRINT",EDGE,{"derivedFrom":sQuery(id+"F61.wireOp",EDGE,"E120")}),1.0]])]});
            var Q7;
            Q7=makeQuery(id+"F61.imprint","IMPRINT",FACE,{"disambiguationData":[TD([[makeQuery(id+"F61.imprint","IMPRINT",EDGE,{"derivedFrom":sQuery(id+"F61.wireOp",EDGE,"E124")}),1.0]])]});
            var Q8;
            Q8=makeQuery(id+"F61.imprint","IMPRINT",FACE,{"disambiguationData":[TD([[makeQuery(id+"F61.imprint","IMPRINT",EDGE,{"derivedFrom":sQuery(id+"F61.wireOp",EDGE,"E121")}),1.0]])]});
            extrude(context, id + "F62", {"entities" : qUnion([Q0, Q1, Q2, Q3, Q4, Q5, Q6, Q7, Q8]), "operationType" : NewBodyOperationType.REMOVE, "oppositeDirection" : true, "depth" : 0.4 * mm, "offsetDistance" : 25.4 * mm});
        }
        {
            var Q0;
            {var subQ0=sQuery(id+"F0.wireOp",EDGE,"E0.bottom");Q0=makeQuery(id+"F5.boolean.opBoolean","MERGE",FACE,{"derivedFrom":[makeQuery(id+"F1.opExtrude","SWEPT_FACE",FACE,{"disambiguationData":[OSD([subQ0])]}),makeQuery(id+"F5.opExtrude","SWEPT_FACE",FACE,{"disambiguationData":[OSD([subQ0])]})]});}
            var sketch = newSketch(context, id + "F63", { "sketchPlane" : qUnion([Q0])});
            skLineSegment(sketch, "E126.bottom", {"start": v(-8.04, 12.7) * mm, "end": v(-1.7, 12.7) * mm});
            skLineSegment(sketch, "E126.top", {"start": v(-8.04, 9.53) * mm, "end": v(-1.7, 9.53) * mm});
            skLineSegment(sketch, "E126.left", {"start": v(-8.04, 12.7) * mm, "end": v(-8.04, 9.53) * mm});
            skLineSegment(sketch, "E126.right", {"start": v(-1.7, 12.7) * mm, "end": v(-1.7, 9.53) * mm});
            skSolve(sketch);
        }
        {
            var Q0;
            Q0=makeQuery(id+"F63.imprint","IMPRINT",FACE,{"disambiguationData":[TD([[makeQuery(id+"F63.imprint","IMPRINT",EDGE,{"derivedFrom":sQuery(id+"F63.wireOp",EDGE,"E126.bottom")}),1.0]])]});
            extrude(context, id + "F64", {"entities" : qUnion([Q0]), "operationType" : NewBodyOperationType.REMOVE, "oppositeDirection" : true, "depth" : 2.54 * mm, "offsetDistance" : 25.4 * mm});
        }
        {
            var Q0;
            {var subQ0=sQuery(id+"F0.wireOp",EDGE,"E0.top");Q0=makeQuery(id+"F5.boolean.opBoolean","MERGE",FACE,{"derivedFrom":[makeQuery(id+"F1.opExtrude","SWEPT_FACE",FACE,{"disambiguationData":[OSD([subQ0])]}),makeQuery(id+"F5.opExtrude","SWEPT_FACE",FACE,{"disambiguationData":[OSD([subQ0])]})]});}
            var sketch = newSketch(context, id + "F65", { "sketchPlane" : qUnion([Q0])});
            skLineSegment(sketch, "E127.bottom", {"start": v(4.01, 12.7) * mm, "end": v(0.84, 12.7) * mm});
            skLineSegment(sketch, "E127.top", {"start": v(4.01, 0) * mm, "end": v(0.84, 0) * mm});
            skLineSegment(sketch, "E127.left", {"start": v(4.01, 12.7) * mm, "end": v(4.01, 0) * mm});
            skLineSegment(sketch, "E127.right", {"start": v(0.84, 12.7) * mm, "end": v(0.84, 0) * mm});
            skSolve(sketch);
        }
        {
            var Q0;
            Q0=makeQuery(id+"F65.imprint","IMPRINT",FACE,{"disambiguationData":[TD([[makeQuery(id+"F65.imprint","IMPRINT",EDGE,{"derivedFrom":sQuery(id+"F65.wireOp",EDGE,"E127.bottom")}),-1.0]])]});
            extrude(context, id + "F66", {"entities" : qUnion([Q0]), "operationType" : NewBodyOperationType.REMOVE, "oppositeDirection" : true, "depth" : 1.27 * mm, "offsetDistance" : 25.4 * mm});
        }
        {
            var Q0;
            {var subQ0=sQuery(id+"F0.wireOp",EDGE,"E0.left");Q0=makeQuery(id+"F5.boolean.opBoolean","MERGE",FACE,{"derivedFrom":[makeQuery(id+"F1.opExtrude","SWEPT_FACE",FACE,{"disambiguationData":[OSD([subQ0])]}),makeQuery(id+"F5.opExtrude","SWEPT_FACE",FACE,{"disambiguationData":[OSD([subQ0])]})]});}
            var sketch = newSketch(context, id + "F67", { "sketchPlane" : qUnion([Q0])});
            skLineSegment(sketch, "E128.top", {"start": v(3.18, 9.53) * mm, "end": v(-3.17, 9.53) * mm});
            skLineSegment(sketch, "E128.left", {"start": v(3.18, 15.88) * mm, "end": v(3.18, 9.53) * mm});
            skLineSegment(sketch, "E128.right", {"start": v(-3.17, 15.88) * mm, "end": v(-3.17, 9.53) * mm});
            skPoint(sketch, "E128.middle", {"position": v(0, 12.7) * mm});
            skSolve(sketch);
        }
        {
            var Q0;
            {var subQ0=sQuery(id+"F67.wireOp",EDGE,"E128.bottom");Q0=makeQuery(id+"F67.imprint","IMPRINT",FACE,{"disambiguationData":[TD([[makeQuery(id+"F67.imprint","IMPRINT",EDGE,{"derivedFrom":subQ0}),1.0]])]});}
            var Q1;
            {var subQ0=sQuery(id+"F67.wireOp",EDGE,"E128.top");Q1=makeQuery(id+"F67.imprint","IMPRINT",FACE,{"disambiguationData":[TD([[makeQuery(id+"F67.imprint","IMPRINT",EDGE,{"derivedFrom":subQ0}),-1.0]])]});}
            extrude(context, id + "F68", {"entities" : qUnion([Q0, Q1]), "operationType" : NewBodyOperationType.REMOVE, "endBound" : BoundingType.THROUGH_ALL, "oppositeDirection" : true, "depth" : 25.4 * mm, "offsetDistance" : 25.4 * mm});
        }
        {
            var Q0;
            {var subQ7=sQuery(id+"F0.wireOp",EDGE,"E0.top");Q0=makeQuery(id+"F66.boolean.opBoolean","SPLIT",FACE,{"disambiguationData":[TD([makeQuery(id+"F66.opExtrude","SWEPT_FACE",FACE,{"disambiguationData":[OSD([sQuery(id+"F65.wireOp",EDGE,"E127.left")])]})])],"derivedFrom":makeQuery(id+"F5.boolean.opBoolean","MERGE",FACE,{"derivedFrom":[makeQuery(id+"F1.opExtrude","SWEPT_FACE",FACE,{"disambiguationData":[OSD([subQ7])]}),makeQuery(id+"F5.opExtrude","SWEPT_FACE",FACE,{"disambiguationData":[OSD([subQ7])]})]})});}
            var sketch = newSketch(context, id + "F69", { "sketchPlane" : qUnion([Q0])});
            skLineSegment(sketch, "E129.bottom", {"start": v(132.57, 11.1) * mm, "end": v(140.5, 11.1) * mm});
            skLineSegment(sketch, "E129.top", {"start": v(132.57, 0) * mm, "end": v(140.5, 0) * mm});
            skLineSegment(sketch, "E129.left", {"start": v(132.57, 11.1) * mm, "end": v(132.57, 0) * mm});
            skLineSegment(sketch, "E129.right", {"start": v(140.5, 11.1) * mm, "end": v(140.5, 0) * mm});
            skLineSegment(sketch, "E130.bottom", {"start": v(55.43, 11.1) * mm, "end": v(63.37, 11.1) * mm});
            skLineSegment(sketch, "E130.top", {"start": v(55.43, 0) * mm, "end": v(63.37, 0) * mm});
            skLineSegment(sketch, "E130.left", {"start": v(55.43, 11.1) * mm, "end": v(55.43, 0) * mm});
            skLineSegment(sketch, "E130.right", {"start": v(63.37, 11.1) * mm, "end": v(63.37, 0) * mm});
            skLineSegment(sketch, "E131.bottom", {"start": v(-91.79, 11.1) * mm, "end": v(-83.85, 11.1) * mm});
            skLineSegment(sketch, "E131.top", {"start": v(-91.79, 0) * mm, "end": v(-83.85, 0) * mm});
            skLineSegment(sketch, "E131.left", {"start": v(-91.79, 11.1) * mm, "end": v(-91.79, 0) * mm});
            skLineSegment(sketch, "E131.right", {"start": v(-83.85, 11.1) * mm, "end": v(-83.85, 0) * mm});
            skLineSegment(sketch, "E132.bottom", {"start": v(-114.17, 11.1) * mm, "end": v(-106.23, 11.1) * mm});
            skLineSegment(sketch, "E132.top", {"start": v(-114.17, 0) * mm, "end": v(-106.23, 0) * mm});
            skLineSegment(sketch, "E132.left", {"start": v(-114.17, 11.1) * mm, "end": v(-114.17, 0) * mm});
            skLineSegment(sketch, "E132.right", {"start": v(-106.23, 11.1) * mm, "end": v(-106.23, 0) * mm});
            skSolve(sketch);
        }
        {
            var Q0;
            Q0=makeQuery(id+"F69.imprint","IMPRINT",FACE,{"disambiguationData":[TD([[makeQuery(id+"F69.imprint","IMPRINT",EDGE,{"derivedFrom":sQuery(id+"F69.wireOp",EDGE,"E132.bottom")}),-1.0]])]});
            var Q1;
            Q1=makeQuery(id+"F69.imprint","IMPRINT",FACE,{"disambiguationData":[TD([[makeQuery(id+"F69.imprint","IMPRINT",EDGE,{"derivedFrom":sQuery(id+"F69.wireOp",EDGE,"E131.bottom")}),-1.0]])]});
            var Q2;
            Q2=makeQuery(id+"F69.imprint","IMPRINT",FACE,{"disambiguationData":[TD([[makeQuery(id+"F69.imprint","IMPRINT",EDGE,{"derivedFrom":sQuery(id+"F69.wireOp",EDGE,"E130.bottom")}),-1.0]])]});
            var Q3;
            Q3=makeQuery(id+"F69.imprint","IMPRINT",FACE,{"disambiguationData":[TD([[makeQuery(id+"F69.imprint","IMPRINT",EDGE,{"derivedFrom":sQuery(id+"F69.wireOp",EDGE,"E129.bottom")}),-1.0]])]});
            extrude(context, id + "F70", {"entities" : qUnion([Q0, Q1, Q2, Q3]), "operationType" : NewBodyOperationType.REMOVE, "oppositeDirection" : true, "depth" : 1.6 * mm, "offsetDistance" : 25.4 * mm});
        }
        {
            var Q0;
            Q0=makeQuery(id+"F70.boolean.opBoolean","COPY",EDGE,{"derivedFrom":makeQuery(id+"F70.opExtrude","CAP_EDGE",EDGE,{"disambiguationData":[OSD([sQuery(id+"F69.wireOp",EDGE,"E132.left")])],"isStart":false})});
            var Q1;
            Q1=makeQuery(id+"F70.boolean.opBoolean","COPY",EDGE,{"derivedFrom":makeQuery(id+"F70.opExtrude","CAP_EDGE",EDGE,{"disambiguationData":[OSD([sQuery(id+"F69.wireOp",EDGE,"E131.left")])],"isStart":false})});
            var Q2;
            Q2=makeQuery(id+"F70.boolean.opBoolean","COPY",EDGE,{"derivedFrom":makeQuery(id+"F70.opExtrude","CAP_EDGE",EDGE,{"disambiguationData":[OSD([sQuery(id+"F69.wireOp",EDGE,"E130.left")])],"isStart":false})});
            var Q3;
            Q3=makeQuery(id+"F70.boolean.opBoolean","COPY",EDGE,{"derivedFrom":makeQuery(id+"F70.opExtrude","CAP_EDGE",EDGE,{"disambiguationData":[OSD([sQuery(id+"F69.wireOp",EDGE,"E129.left")])],"isStart":false})});
            var Q4;
            Q4=makeQuery(id+"F70.boolean.opBoolean","COPY",EDGE,{"derivedFrom":makeQuery(id+"F70.opExtrude","CAP_EDGE",EDGE,{"disambiguationData":[OSD([sQuery(id+"F69.wireOp",EDGE,"E129.right")])],"isStart":false})});
            var Q5;
            Q5=makeQuery(id+"F70.boolean.opBoolean","COPY",EDGE,{"derivedFrom":makeQuery(id+"F70.opExtrude","CAP_EDGE",EDGE,{"disambiguationData":[OSD([sQuery(id+"F69.wireOp",EDGE,"E130.right")])],"isStart":false})});
            var Q6;
            Q6=makeQuery(id+"F70.boolean.opBoolean","COPY",EDGE,{"derivedFrom":makeQuery(id+"F70.opExtrude","CAP_EDGE",EDGE,{"disambiguationData":[OSD([sQuery(id+"F69.wireOp",EDGE,"E131.right")])],"isStart":false})});
            var Q7;
            Q7=makeQuery(id+"F70.boolean.opBoolean","COPY",EDGE,{"derivedFrom":makeQuery(id+"F70.opExtrude","CAP_EDGE",EDGE,{"disambiguationData":[OSD([sQuery(id+"F69.wireOp",EDGE,"E132.right")])],"isStart":false})});
            chamfer(context, id + "F71", {"entities" : qUnion([Q0, Q1, Q2, Q3, Q4, Q5, Q6, Q7]), "width" : 1.6 * mm, "tangentPropagation" : true});
        }
        {
            var Q0;
            {var subQ7=sQuery(id+"F0.wireOp",EDGE,"E0.top");Q0=makeQuery(id+"F66.boolean.opBoolean","SPLIT",FACE,{"disambiguationData":[TD([makeQuery(id+"F66.opExtrude","SWEPT_FACE",FACE,{"disambiguationData":[OSD([sQuery(id+"F65.wireOp",EDGE,"E127.left")])]})])],"derivedFrom":makeQuery(id+"F5.boolean.opBoolean","MERGE",FACE,{"derivedFrom":[makeQuery(id+"F1.opExtrude","SWEPT_FACE",FACE,{"disambiguationData":[OSD([subQ7])]}),makeQuery(id+"F5.opExtrude","SWEPT_FACE",FACE,{"disambiguationData":[OSD([subQ7])]})]})});}
            var sketch = newSketch(context, id + "F72", { "sketchPlane" : qUnion([Q0])});
            skCircle(sketch, "E133", {"center": v(148.63, 3.96) * mm, "radius": 3.18 * mm});
            skCircle(sketch, "E134", {"center": v(47.74, 3.96) * mm, "radius": 3.18 * mm});
            skCircle(sketch, "E135", {"center": v(-99.24, 3.96) * mm, "radius": 3.18 * mm});
            skCircle(sketch, "E136", {"center": v(-99.24, 3.96) * mm, "radius": 1.59 * mm});
            skCircle(sketch, "E137", {"center": v(47.74, 3.96) * mm, "radius": 1.59 * mm});
            skCircle(sketch, "E138", {"center": v(148.63, 3.96) * mm, "radius": 1.59 * mm});
            skSolve(sketch);
        }
        {
            var Q0;
            Q0=makeQuery(id+"F72.imprint","IMPRINT",FACE,{"disambiguationData":[TD([[makeQuery(id+"F72.imprint","IMPRINT",EDGE,{"derivedFrom":sQuery(id+"F72.wireOp",EDGE,"E135")}),1.0]])]});
            var Q1;
            Q1=makeQuery(id+"F72.imprint","IMPRINT",FACE,{"disambiguationData":[TD([[makeQuery(id+"F72.imprint","IMPRINT",EDGE,{"derivedFrom":sQuery(id+"F72.wireOp",EDGE,"E134")}),1.0]])]});
            var Q2;
            Q2=makeQuery(id+"F72.imprint","IMPRINT",FACE,{"disambiguationData":[TD([[makeQuery(id+"F72.imprint","IMPRINT",EDGE,{"derivedFrom":sQuery(id+"F72.wireOp",EDGE,"E133")}),1.0]])]});
            extrude(context, id + "F73", {"entities" : qUnion([Q0, Q1, Q2]), "operationType" : NewBodyOperationType.ADD, "depth" : 1.6 * mm, "offsetDistance" : 25.4 * mm});
        }
        {
            var Q0;
            {var subQ7=sQuery(id+"F0.wireOp",EDGE,"E0.top");Q0=makeQuery(id+"F73.boolean.opBoolean","SPLIT",FACE,{"disambiguationData":[TD([makeQuery(id+"F73.opExtrude","SWEPT_FACE",FACE,{"disambiguationData":[OSD([sQuery(id+"F72.wireOp",EDGE,"E136")])]})])],"derivedFrom":makeQuery(id+"F66.boolean.opBoolean","SPLIT",FACE,{"disambiguationData":[TD([makeQuery(id+"F66.opExtrude","SWEPT_FACE",FACE,{"disambiguationData":[OSD([sQuery(id+"F65.wireOp",EDGE,"E127.right")])]})])],"derivedFrom":makeQuery(id+"F5.boolean.opBoolean","MERGE",FACE,{"derivedFrom":[makeQuery(id+"F1.opExtrude","SWEPT_FACE",FACE,{"disambiguationData":[OSD([subQ7])]}),makeQuery(id+"F5.opExtrude","SWEPT_FACE",FACE,{"disambiguationData":[OSD([subQ7])]})]})})});}
            var sketch = newSketch(context, id + "F74", { "sketchPlane" : qUnion([Q0])});
            skCircle(sketch, "E139", {"center": v(-99.24, 3.96) * mm, "radius": 1.27 * mm});
            skSolve(sketch);
        }
        {
            var Q0;
            Q0=makeQuery(id+"F74.imprint","IMPRINT",FACE,{"disambiguationData":[TD([[makeQuery(id+"F74.imprint","IMPRINT",EDGE,{"derivedFrom":sQuery(id+"F74.wireOp",EDGE,"E139")}),1.0]])]});
            extrude(context, id + "F75", {"entities" : qUnion([Q0]), "operationType" : NewBodyOperationType.ADD, "depth" : 2.54 * mm, "offsetDistance" : 25.4 * mm});
        }
        {
            var Q0;
            {var subQ7=sQuery(id+"F0.wireOp",EDGE,"E0.top");Q0=makeQuery(id+"F73.boolean.opBoolean","SPLIT",FACE,{"disambiguationData":[TD([makeQuery(id+"F73.opExtrude","SWEPT_FACE",FACE,{"disambiguationData":[OSD([sQuery(id+"F72.wireOp",EDGE,"E137")])]})])],"derivedFrom":makeQuery(id+"F66.boolean.opBoolean","SPLIT",FACE,{"disambiguationData":[TD([makeQuery(id+"F66.opExtrude","SWEPT_FACE",FACE,{"disambiguationData":[OSD([sQuery(id+"F65.wireOp",EDGE,"E127.left")])]})])],"derivedFrom":makeQuery(id+"F5.boolean.opBoolean","MERGE",FACE,{"derivedFrom":[makeQuery(id+"F1.opExtrude","SWEPT_FACE",FACE,{"disambiguationData":[OSD([subQ7])]}),makeQuery(id+"F5.opExtrude","SWEPT_FACE",FACE,{"disambiguationData":[OSD([subQ7])]})]})})});}
            var sketch = newSketch(context, id + "F76", { "sketchPlane" : qUnion([Q0])});
            skCircle(sketch, "E140", {"center": v(47.74, 3.96) * mm, "radius": 1.27 * mm});
            skSolve(sketch);
        }
        {
            var Q0;
            Q0=makeQuery(id+"F76.imprint","IMPRINT",FACE,{"disambiguationData":[TD([[makeQuery(id+"F76.imprint","IMPRINT",EDGE,{"derivedFrom":sQuery(id+"F76.wireOp",EDGE,"E140")}),1.0]])]});
            extrude(context, id + "F77", {"entities" : qUnion([Q0]), "operationType" : NewBodyOperationType.ADD, "depth" : 2.54 * mm, "offsetDistance" : 25.4 * mm});
        }
        {
            var Q0;
            {var subQ7=sQuery(id+"F0.wireOp",EDGE,"E0.top");Q0=makeQuery(id+"F73.boolean.opBoolean","SPLIT",FACE,{"disambiguationData":[TD([makeQuery(id+"F73.opExtrude","SWEPT_FACE",FACE,{"disambiguationData":[OSD([sQuery(id+"F72.wireOp",EDGE,"E138")])]})])],"derivedFrom":makeQuery(id+"F66.boolean.opBoolean","SPLIT",FACE,{"disambiguationData":[TD([makeQuery(id+"F66.opExtrude","SWEPT_FACE",FACE,{"disambiguationData":[OSD([sQuery(id+"F65.wireOp",EDGE,"E127.left")])]})])],"derivedFrom":makeQuery(id+"F5.boolean.opBoolean","MERGE",FACE,{"derivedFrom":[makeQuery(id+"F1.opExtrude","SWEPT_FACE",FACE,{"disambiguationData":[OSD([subQ7])]}),makeQuery(id+"F5.opExtrude","SWEPT_FACE",FACE,{"disambiguationData":[OSD([subQ7])]})]})})});}
            var sketch = newSketch(context, id + "F78", { "sketchPlane" : qUnion([Q0])});
            skCircle(sketch, "E141", {"center": v(148.63, 3.96) * mm, "radius": 1.27 * mm});
            skSolve(sketch);
        }
        {
            var Q0;
            Q0=makeQuery(id+"F78.imprint","IMPRINT",FACE,{"disambiguationData":[TD([[makeQuery(id+"F78.imprint","IMPRINT",EDGE,{"derivedFrom":sQuery(id+"F78.wireOp",EDGE,"E141")}),1.0]])]});
            extrude(context, id + "F79", {"entities" : qUnion([Q0]), "operationType" : NewBodyOperationType.ADD, "depth" : 2.54 * mm, "offsetDistance" : 25.4 * mm});
        }
        {
            var Q0;
            Q0=qCreatedBy(makeId("Top.planeOp"),FACE);
            var sketch = newSketch(context, id + "F80", { "sketchPlane" : qUnion([Q0])});
            skLineSegment(sketch, "E142.bottom", {"start": v(166.69, -66.76) * mm, "end": v(-166.69, -66.76) * mm});
            skLineSegment(sketch, "E142.top", {"start": v(166.69, -193.76) * mm, "end": v(-166.69, -193.76) * mm});
            skLineSegment(sketch, "E142.left", {"start": v(166.69, -66.76) * mm, "end": v(166.69, -193.76) * mm});
            skLineSegment(sketch, "E142.right", {"start": v(-166.69, -66.76) * mm, "end": v(-166.69, -193.76) * mm});
            skPoint(sketch, "E142.middle", {"position": v(0, -130.26) * mm});
            skLineSegment(sketch, "E143.bottom", {"start": v(-106.36, -66.76) * mm, "end": v(-90.49, -66.76) * mm});
            skLineSegment(sketch, "E143.top", {"start": v(-106.36, -57.23) * mm, "end": v(-90.49, -57.23) * mm});
            skLineSegment(sketch, "E143.left", {"start": v(-106.36, -66.76) * mm, "end": v(-106.36, -57.23) * mm});
            skLineSegment(sketch, "E143.right", {"start": v(-90.49, -66.76) * mm, "end": v(-90.49, -57.23) * mm});
            skLineSegment(sketch, "E144.bottom", {"start": v(90.49, -66.76) * mm, "end": v(106.36, -66.76) * mm});
            skLineSegment(sketch, "E144.top", {"start": v(90.49, -57.23) * mm, "end": v(106.36, -57.23) * mm});
            skLineSegment(sketch, "E144.left", {"start": v(90.49, -66.76) * mm, "end": v(90.49, -57.23) * mm});
            skLineSegment(sketch, "E144.right", {"start": v(106.36, -66.76) * mm, "end": v(106.36, -57.23) * mm});
            skSolve(sketch);
        }
        {
            var Q0;
            Q0=makeQuery(id+"F80.imprint","IMPRINT",FACE,{"disambiguationData":[TD([[makeQuery(id+"F80.imprint","IMPRINT",EDGE,{"derivedFrom":sQuery(id+"F80.wireOp",EDGE,"E143.top")}),-1.0]])]});
            var Q1;
            Q1=makeQuery(id+"F80.imprint","IMPRINT",FACE,{"disambiguationData":[TD([[makeQuery(id+"F80.imprint","IMPRINT",EDGE,{"derivedFrom":sQuery(id+"F80.wireOp",EDGE,"E144.top")}),-1.0]])]});
            var Q2;
            Q2=makeQuery(id+"F80.imprint","IMPRINT",FACE,{"disambiguationData":[TD([[makeQuery(id+"F80.imprint","IMPRINT",EDGE,{"derivedFrom":sQuery(id+"F80.wireOp",EDGE,"E142.top")}),-1.0]])]});
            extrude(context, id + "F81", {"entities" : qUnion([Q0, Q1, Q2]), "depth" : 2.38 * mm, "offsetDistance" : 25.4 * mm});
        }
        {
            var Q0;
            Q0=makeQuery(id+"F81.opExtrude","CAP_FACE",FACE,{"disambiguationData":[OSD([sQuery(id+"F80.wireOp",EDGE,"E142.bottom"),sQuery(id+"F80.wireOp",EDGE,"E142.top"),sQuery(id+"F80.wireOp",EDGE,"E142.left"),sQuery(id+"F80.wireOp",EDGE,"E142.right"),sQuery(id+"F80.wireOp",EDGE,"E143.top"),sQuery(id+"F80.wireOp",EDGE,"E143.left"),sQuery(id+"F80.wireOp",EDGE,"E143.right"),sQuery(id+"F80.wireOp",EDGE,"E144.top"),sQuery(id+"F80.wireOp",EDGE,"E144.left"),sQuery(id+"F80.wireOp",EDGE,"E144.right")])],"isStart":false});
            var sketch = newSketch(context, id + "F82", { "sketchPlane" : qUnion([Q0])});
            skPoint(sketch, "E145.oppositeSnap0", {"position": v(-90.49, -62) * mm});
            skLineSegment(sketch, "E145.bottom", {"start": v(-106.36, -57.23) * mm, "end": v(-90.49, -57.23) * mm});
            skLineSegment(sketch, "E145.top", {"start": v(-106.36, -73.1) * mm, "end": v(-90.49, -73.1) * mm});
            skLineSegment(sketch, "E145.left", {"start": v(-106.36, -57.23) * mm, "end": v(-106.36, -73.1) * mm});
            skLineSegment(sketch, "E145.right", {"start": v(-90.49, -57.23) * mm, "end": v(-90.49, -73.1) * mm});
            skLineSegment(sketch, "E146.bottom", {"start": v(106.36, -57.23) * mm, "end": v(90.49, -57.23) * mm});
            skLineSegment(sketch, "E146.top", {"start": v(106.36, -73.1) * mm, "end": v(90.49, -73.1) * mm});
            skLineSegment(sketch, "E146.left", {"start": v(106.36, -57.23) * mm, "end": v(106.36, -73.1) * mm});
            skLineSegment(sketch, "E146.right", {"start": v(90.49, -57.23) * mm, "end": v(90.49, -73.1) * mm});
            skLineSegment(sketch, "E147", {"start": v(92.07, -73.1) * mm, "end": v(92.07, -62) * mm});
            skLineSegment(sketch, "E148", {"start": v(92.07, -62) * mm, "end": v(93.66, -62) * mm});
            skLineSegment(sketch, "E149", {"start": v(93.66, -62) * mm, "end": v(93.66, -70.72) * mm});
            skLineSegment(sketch, "E150", {"start": v(93.66, -70.72) * mm, "end": v(103.19, -70.72) * mm});
            skLineSegment(sketch, "E151", {"start": v(103.19, -70.72) * mm, "end": v(103.19, -62) * mm});
            skLineSegment(sketch, "E152", {"start": v(103.19, -62) * mm, "end": v(104.77, -62) * mm});
            skLineSegment(sketch, "E153", {"start": v(104.77, -62) * mm, "end": v(104.77, -73.1) * mm});
            skLineSegment(sketch, "E154", {"start": v(-104.76, -73.1) * mm, "end": v(-104.76, -62) * mm});
            skLineSegment(sketch, "E155", {"start": v(-104.76, -62) * mm, "end": v(-103.16, -62) * mm});
            skLineSegment(sketch, "E156", {"start": v(-103.16, -62) * mm, "end": v(-103.16, -70.72) * mm});
            skLineSegment(sketch, "E157", {"start": v(-103.16, -70.72) * mm, "end": v(-93.69, -70.72) * mm});
            skLineSegment(sketch, "E158", {"start": v(-93.69, -70.72) * mm, "end": v(-93.69, -62) * mm});
            skLineSegment(sketch, "E159", {"start": v(-93.69, -62) * mm, "end": v(-92.09, -62) * mm});
            skLineSegment(sketch, "E160", {"start": v(-92.09, -62) * mm, "end": v(-92.09, -73.1) * mm});
            skSolve(sketch);
        }
        {
            var Q0;
            {var subQ9=sQuery(id+"F82.wireOp",EDGE,"E145.bottom");Q0=makeQuery(id+"F82.imprint","IMPRINT",FACE,{"disambiguationData":[TD([[makeQuery(id+"F82.imprint","IMPRINT",EDGE,{"derivedFrom":subQ9}),-1.0]])]});}
            var Q1;
            {var subQ7=sQuery(id+"F82.wireOp",EDGE,"E146.bottom");Q1=makeQuery(id+"F82.imprint","IMPRINT",FACE,{"disambiguationData":[TD([[makeQuery(id+"F82.imprint","IMPRINT",EDGE,{"derivedFrom":subQ7}),-1.0]])]});}
            extrude(context, id + "F83", {"entities" : qUnion([Q0, Q1]), "operationType" : NewBodyOperationType.ADD, "depth" : 1.59 * mm, "offsetDistance" : 25.4 * mm});
        }
        {
            var Q0;
            Q0=makeQuery(id+"F83.opExtrude","CAP_EDGE",EDGE,{"disambiguationData":[OSD([sQuery(id+"F82.wireOp",EDGE,"E157")])],"isStart":false});
            var Q1;
            Q1=makeQuery(id+"F83.opExtrude","CAP_EDGE",EDGE,{"disambiguationData":[OSD([sQuery(id+"F82.wireOp",EDGE,"E150")])],"isStart":false});
            var Q2;
            Q2=makeQuery(id+"F83.opExtrude","CAP_EDGE",EDGE,{"disambiguationData":[OSD([sQuery(id+"F82.wireOp",EDGE,"E148")])],"isStart":true});
            var Q3;
            Q3=makeQuery(id+"F83.opExtrude","CAP_EDGE",EDGE,{"disambiguationData":[OSD([sQuery(id+"F82.wireOp",EDGE,"E152")])],"isStart":true});
            var Q4;
            Q4=makeQuery(id+"F83.opExtrude","CAP_EDGE",EDGE,{"disambiguationData":[OSD([sQuery(id+"F82.wireOp",EDGE,"E159")])],"isStart":true});
            var Q5;
            Q5=makeQuery(id+"F83.opExtrude","CAP_EDGE",EDGE,{"disambiguationData":[OSD([sQuery(id+"F82.wireOp",EDGE,"E155")])],"isStart":true});
            chamfer(context, id + "F84", {"entities" : qUnion([Q0, Q1, Q2, Q3, Q4, Q5]), "width" : 1.65 * mm, "tangentPropagation" : true});
        }
        {
            var Q0;
            Q0=makeQuery(id+"F83.boolean.opBoolean","MERGE",EDGE,{"derivedFrom":[makeQuery(id+"F81.opExtrude","SWEPT_EDGE",EDGE,{"disambiguationData":[OSD([sQuery(id+"F80.wireOp",EDGE,"E143.top"),sQuery(id+"F80.wireOp",EDGE,"E143.left")])]}),makeQuery(id+"F83.opExtrude","SWEPT_EDGE",EDGE,{"disambiguationData":[OSD([sQuery(id+"F82.wireOp",EDGE,"E145.bottom"),sQuery(id+"F82.wireOp",EDGE,"E145.left")])]})]});
            var Q1;
            Q1=makeQuery(id+"F83.boolean.opBoolean","MERGE",EDGE,{"derivedFrom":[makeQuery(id+"F81.opExtrude","SWEPT_EDGE",EDGE,{"disambiguationData":[OSD([sQuery(id+"F80.wireOp",EDGE,"E143.top"),sQuery(id+"F80.wireOp",EDGE,"E143.right")])]}),makeQuery(id+"F83.opExtrude","SWEPT_EDGE",EDGE,{"disambiguationData":[OSD([sQuery(id+"F82.wireOp",EDGE,"E145.bottom"),sQuery(id+"F82.wireOp",EDGE,"E145.right")])]})]});
            var Q2;
            Q2=makeQuery(id+"F83.boolean.opBoolean","MERGE",EDGE,{"derivedFrom":[makeQuery(id+"F81.opExtrude","SWEPT_EDGE",EDGE,{"disambiguationData":[OSD([sQuery(id+"F80.wireOp",EDGE,"E144.top"),sQuery(id+"F80.wireOp",EDGE,"E144.right")])]}),makeQuery(id+"F83.opExtrude","SWEPT_EDGE",EDGE,{"disambiguationData":[OSD([sQuery(id+"F82.wireOp",EDGE,"E146.bottom"),sQuery(id+"F82.wireOp",EDGE,"E146.left")])]})]});
            var Q3;
            Q3=makeQuery(id+"F83.boolean.opBoolean","MERGE",EDGE,{"derivedFrom":[makeQuery(id+"F81.opExtrude","SWEPT_EDGE",EDGE,{"disambiguationData":[OSD([sQuery(id+"F80.wireOp",EDGE,"E144.top"),sQuery(id+"F80.wireOp",EDGE,"E144.left")])]}),makeQuery(id+"F83.opExtrude","SWEPT_EDGE",EDGE,{"disambiguationData":[OSD([sQuery(id+"F82.wireOp",EDGE,"E146.bottom"),sQuery(id+"F82.wireOp",EDGE,"E146.right")])]})]});
            chamfer(context, id + "F85", {"entities" : qUnion([Q0, Q1, Q2, Q3]), "width" : 1.9 * mm, "tangentPropagation" : true});
        }
        {
            var Q0;
            Q0=makeQuery(id+"F83.opExtrude","CAP_FACE",FACE,{"disambiguationData":[OSD([sQuery(id+"F82.wireOp",EDGE,"E145.bottom"),sQuery(id+"F82.wireOp",EDGE,"E145.top"),sQuery(id+"F82.wireOp",EDGE,"E145.left"),sQuery(id+"F82.wireOp",EDGE,"E145.right"),sQuery(id+"F82.wireOp",EDGE,"E154"),sQuery(id+"F82.wireOp",EDGE,"E155"),sQuery(id+"F82.wireOp",EDGE,"E156"),sQuery(id+"F82.wireOp",EDGE,"E157"),sQuery(id+"F82.wireOp",EDGE,"E158"),sQuery(id+"F82.wireOp",EDGE,"E159"),sQuery(id+"F82.wireOp",EDGE,"E160")])],"isStart":false});
            var sketch = newSketch(context, id + "F86", { "sketchPlane" : qUnion([Q0])});
            skCircle(sketch, "E161", {"center": v(-98.43, -62.8) * mm, "radius": 2.39 * mm});
            skSolve(sketch);
        }
        {
            var Q0;
            Q0=makeQuery(id+"F86.imprint","IMPRINT",FACE,{"disambiguationData":[TD([[makeQuery(id+"F86.imprint","IMPRINT",EDGE,{"derivedFrom":sQuery(id+"F86.wireOp",EDGE,"E161")}),1.0]])]});
            extrude(context, id + "F87", {"entities" : qUnion([Q0]), "operationType" : NewBodyOperationType.REMOVE, "endBound" : BoundingType.THROUGH_ALL, "oppositeDirection" : true, "depth" : 25.4 * mm, "offsetDistance" : 25.4 * mm});
        }
        {
            var Q0;
            Q0=makeQuery(id+"F83.opExtrude","CAP_FACE",FACE,{"disambiguationData":[OSD([sQuery(id+"F82.wireOp",EDGE,"E146.bottom"),sQuery(id+"F82.wireOp",EDGE,"E146.top"),sQuery(id+"F82.wireOp",EDGE,"E146.left"),sQuery(id+"F82.wireOp",EDGE,"E146.right"),sQuery(id+"F82.wireOp",EDGE,"E147"),sQuery(id+"F82.wireOp",EDGE,"E148"),sQuery(id+"F82.wireOp",EDGE,"E149"),sQuery(id+"F82.wireOp",EDGE,"E150"),sQuery(id+"F82.wireOp",EDGE,"E151"),sQuery(id+"F82.wireOp",EDGE,"E152"),sQuery(id+"F82.wireOp",EDGE,"E153")])],"isStart":false});
            var sketch = newSketch(context, id + "F88", { "sketchPlane" : qUnion([Q0])});
            skCircle(sketch, "E162", {"center": v(98.42, -62.8) * mm, "radius": 2.39 * mm});
            skPoint(sketch, "E162.centerSnap0", {"position": v(98.42, -57.23) * mm});
            skSolve(sketch);
        }
        {
            var Q0;
            Q0=makeQuery(id+"F88.imprint","IMPRINT",FACE,{"disambiguationData":[TD([[makeQuery(id+"F88.imprint","IMPRINT",EDGE,{"derivedFrom":sQuery(id+"F88.wireOp",EDGE,"E162")}),1.0]])]});
            extrude(context, id + "F89", {"entities" : qUnion([Q0]), "operationType" : NewBodyOperationType.REMOVE, "endBound" : BoundingType.THROUGH_ALL, "oppositeDirection" : true, "depth" : 25.4 * mm, "offsetDistance" : 25.4 * mm});
        }
        {
            var Q0;
            Q0=makeQuery(id+"F81.opExtrude","SWEPT_EDGE",EDGE,{"disambiguationData":[OSD([sQuery(id+"F80.wireOp",EDGE,"E142.top"),sQuery(id+"F80.wireOp",EDGE,"E142.right")])]});
            var Q1;
            Q1=makeQuery(id+"F81.opExtrude","SWEPT_EDGE",EDGE,{"disambiguationData":[OSD([sQuery(id+"F80.wireOp",EDGE,"E142.top"),sQuery(id+"F80.wireOp",EDGE,"E142.left")])]});
            fillet(context, id + "F90", {"entities" : qUnion([Q0, Q1]), "radius" : 15.88 * mm, "tangentPropagation" : true, "allowEdgeOverflow" : false});
        }
        {
            var Q0;
            Q0=makeQuery(id+"F81.opExtrude","SWEPT_EDGE",EDGE,{"disambiguationData":[OSD([sQuery(id+"F80.wireOp",EDGE,"E142.bottom"),sQuery(id+"F80.wireOp",EDGE,"E142.right")])]});
            var Q1;
            Q1=makeQuery(id+"F81.opExtrude","SWEPT_EDGE",EDGE,{"disambiguationData":[OSD([sQuery(id+"F80.wireOp",EDGE,"E142.bottom"),sQuery(id+"F80.wireOp",EDGE,"E142.left")])]});
            fillet(context, id + "F91", {"entities" : qUnion([Q0, Q1]), "radius" : 9.52 * mm, "tangentPropagation" : true, "allowEdgeOverflow" : false});
        }
        {
            var Q0;
            Q0=qCreatedBy(makeId("Right.planeOp"),FACE);
            var sketch = newSketch(context, id + "F92", { "sketchPlane" : qUnion([Q0])});
            skLineSegment(sketch, "E163", {"start": v(128.21, 0) * mm, "end": v(242.51, 0) * mm});
            skLineSegment(sketch, "E164", {"start": v(242.51, 0) * mm, "end": v(218.47, 39.26) * mm});
            skLineSegment(sketch, "E165", {"start": v(218.47, 39.26) * mm, "end": v(242.51, 0) * mm, "construction": true});
            skLineSegment(sketch, "E166", {"start": v(218.47, 39.26) * mm, "end": v(128.21, 0) * mm});
            skSolve(sketch);
        }
        {
            var Q0;
            Q0=makeQuery(id+"F92.imprint","IMPRINT",FACE,{"disambiguationData":[TD([[makeQuery(id+"F92.imprint","IMPRINT",EDGE,{"derivedFrom":sQuery(id+"F92.wireOp",EDGE,"E163")}),1.0]])]});
            extrude(context, id + "F93", {"entities" : qUnion([Q0]), "oppositeDirection" : true, "depth" : 323.85 * mm, "offsetDistance" : 25.4 * mm});
        }
        {
            var Q0;
            Q0=makeQuery(id+"F93.opExtrude","CAP_EDGE",EDGE,{"disambiguationData":[OSD([sQuery(id+"F92.wireOp",EDGE,"E164")])],"isStart":true});
            var Q1;
            Q1=makeQuery(id+"F93.opExtrude","CAP_EDGE",EDGE,{"disambiguationData":[OSD([sQuery(id+"F92.wireOp",EDGE,"E164")])],"isStart":false});
            fillet(context, id + "F94", {"entities" : qUnion([Q0, Q1]), "radius" : 9.52 * mm, "tangentPropagation" : true, "allowEdgeOverflow" : false});
        }
        {
            var Q0;
            Q0=makeQuery(id+"F93.opExtrude","SWEPT_FACE",FACE,{"disambiguationData":[OSD([sQuery(id+"F92.wireOp",EDGE,"E164")])]});
            var sketch = newSketch(context, id + "F95", { "sketchPlane" : qUnion([Q0])});
            skLineSegment(sketch, "E167", {"start": v(55.56, -80.62) * mm, "end": v(50.8, -117.13) * mm});
            skLineSegment(sketch, "E168", {"start": v(50.8, -117.13) * mm, "end": v(101.6, -117.13) * mm});
            skLineSegment(sketch, "E169", {"start": v(101.6, -117.13) * mm, "end": v(96.84, -80.62) * mm});
            skLineSegment(sketch, "E170", {"start": v(96.84, -80.62) * mm, "end": v(55.56, -80.62) * mm});
            skLineSegment(sketch, "E171", {"start": v(76.2, -117.13) * mm, "end": v(76.2, -80.62) * mm, "construction": true});
            skLineSegment(sketch, "E172", {"start": v(50.8, -117.13) * mm, "end": v(50.8, -84.8) * mm, "construction": true});
            skLineSegment(sketch, "E173", {"start": v(101.6, -117.13) * mm, "end": v(101.6, -56.53) * mm, "construction": true});
            skLineSegment(sketch, "E174", {"start": v(198.45, -80.62) * mm, "end": v(193.67, -117.13) * mm});
            skLineSegment(sketch, "E175", {"start": v(193.67, -117.13) * mm, "end": v(244.47, -117.13) * mm});
            skLineSegment(sketch, "E176", {"start": v(244.48, -117.13) * mm, "end": v(239.7, -80.62) * mm});
            skLineSegment(sketch, "E177", {"start": v(239.7, -80.62) * mm, "end": v(198.45, -80.62) * mm});
            skLineSegment(sketch, "E178", {"start": v(193.67, -117.13) * mm, "end": v(193.67, -89.33) * mm, "construction": true});
            skLineSegment(sketch, "E179", {"start": v(244.48, -117.13) * mm, "end": v(244.48, -53.54) * mm, "construction": true});
            skLineSegment(sketch, "E180", {"start": v(311.15, -80.62) * mm, "end": v(311.15, -117.13) * mm});
            skLineSegment(sketch, "E181", {"start": v(311.15, -117.13) * mm, "end": v(273.05, -117.13) * mm});
            skLineSegment(sketch, "E182", {"start": v(273.05, -117.13) * mm, "end": v(277.83, -80.62) * mm});
            skLineSegment(sketch, "E183", {"start": v(277.83, -80.62) * mm, "end": v(311.15, -80.62) * mm});
            skLineSegment(sketch, "E184", {"start": v(273.05, -117.13) * mm, "end": v(273.05, -50.37) * mm, "construction": true});
            skSolve(sketch);
        }
        {
            var Q0;
            Q0=makeQuery(id+"F95.imprint","IMPRINT",FACE,{"disambiguationData":[TD([[makeQuery(id+"F95.imprint","IMPRINT",EDGE,{"derivedFrom":sQuery(id+"F95.wireOp",EDGE,"E167")}),1.0]])]});
            var Q1;
            Q1=makeQuery(id+"F95.imprint","IMPRINT",FACE,{"disambiguationData":[TD([[makeQuery(id+"F95.imprint","IMPRINT",EDGE,{"derivedFrom":sQuery(id+"F95.wireOp",EDGE,"E174")}),1.0]])]});
            var Q2;
            Q2=makeQuery(id+"F95.imprint","IMPRINT",FACE,{"disambiguationData":[TD([[makeQuery(id+"F95.imprint","IMPRINT",EDGE,{"derivedFrom":sQuery(id+"F95.wireOp",EDGE,"E180")}),-1.0]])]});
            extrude(context, id + "F96", {"entities" : qUnion([Q0, Q1, Q2]), "operationType" : NewBodyOperationType.REMOVE, "oppositeDirection" : true, "depth" : 5.5 * mm, "offsetDistance" : 25.4 * mm});
        }
        {
            var Q0;
            Q0=makeQuery(id+"F96.boolean.opBoolean","COPY",EDGE,{"derivedFrom":makeQuery(id+"F96.opExtrude","CAP_EDGE",EDGE,{"disambiguationData":[OSD([sQuery(id+"F95.wireOp",EDGE,"E167")])],"isStart":false})});
            var Q1;
            Q1=makeQuery(id+"F96.boolean.opBoolean","COPY",EDGE,{"derivedFrom":makeQuery(id+"F96.opExtrude","CAP_EDGE",EDGE,{"disambiguationData":[OSD([sQuery(id+"F95.wireOp",EDGE,"E169")])],"isStart":false})});
            var Q2;
            Q2=makeQuery(id+"F96.boolean.opBoolean","COPY",EDGE,{"derivedFrom":makeQuery(id+"F96.opExtrude","CAP_EDGE",EDGE,{"disambiguationData":[OSD([sQuery(id+"F95.wireOp",EDGE,"E176")])],"isStart":false})});
            var Q3;
            Q3=makeQuery(id+"F96.boolean.opBoolean","COPY",EDGE,{"derivedFrom":makeQuery(id+"F96.opExtrude","CAP_EDGE",EDGE,{"disambiguationData":[OSD([sQuery(id+"F95.wireOp",EDGE,"E174")])],"isStart":false})});
            var Q4;
            Q4=makeQuery(id+"F96.boolean.opBoolean","COPY",EDGE,{"derivedFrom":makeQuery(id+"F96.opExtrude","CAP_EDGE",EDGE,{"disambiguationData":[OSD([sQuery(id+"F95.wireOp",EDGE,"E182")])],"isStart":false})});
            fillet(context, id + "F97", {"entities" : qUnion([Q0, Q1, Q2, Q3, Q4]), "radius" : 22.86 * mm, "tangentPropagation" : true, "allowEdgeOverflow" : false});
        }
        {
            var Q0;
            Q0=makeQuery(id+"F96.boolean.opBoolean","COPY",EDGE,{"derivedFrom":makeQuery(id+"F96.opExtrude","CAP_EDGE",EDGE,{"disambiguationData":[OSD([sQuery(id+"F95.wireOp",EDGE,"E180")])],"isStart":false})});
            fillet(context, id + "F98", {"entities" : qUnion([Q0]), "radius" : 5.08 * mm, "tangentPropagation" : true, "allowEdgeOverflow" : false});
        }
        {
            var Q0;
            Q0=makeQuery(id+"F96.boolean.opBoolean","COPY",EDGE,{"derivedFrom":makeQuery(id+"F96.opExtrude","CAP_EDGE",EDGE,{"disambiguationData":[OSD([sQuery(id+"F95.wireOp",EDGE,"E175")])],"isStart":false})});
            var Q1;
            Q1=makeQuery(id+"F96.boolean.opBoolean","COPY",EDGE,{"derivedFrom":makeQuery(id+"F96.opExtrude","CAP_EDGE",EDGE,{"disambiguationData":[OSD([sQuery(id+"F95.wireOp",EDGE,"E181")])],"isStart":false})});
            var Q2;
            Q2=makeQuery(id+"F96.boolean.opBoolean","COPY",EDGE,{"derivedFrom":makeQuery(id+"F96.opExtrude","CAP_EDGE",EDGE,{"disambiguationData":[OSD([sQuery(id+"F95.wireOp",EDGE,"E168")])],"isStart":false})});
            fillet(context, id + "F99", {"entities" : qUnion([Q0, Q1, Q2]), "radius" : 5.08 * mm, "tangentPropagation" : true, "allowEdgeOverflow" : false});
        }
        {
            var Q0;
            Q0=makeQuery(id+"F96.boolean.opBoolean","COPY",FACE,{"derivedFrom":makeQuery(id+"F96.opExtrude","SWEPT_FACE",FACE,{"disambiguationData":[OSD([sQuery(id+"F95.wireOp",EDGE,"E170")])]})});
            var Q1;
            Q1=makeQuery(id+"F96.boolean.opBoolean","COPY",FACE,{"derivedFrom":makeQuery(id+"F96.opExtrude","SWEPT_FACE",FACE,{"disambiguationData":[OSD([sQuery(id+"F95.wireOp",EDGE,"E177")])]})});
            var Q2;
            Q2=makeQuery(id+"F96.boolean.opBoolean","COPY",FACE,{"derivedFrom":makeQuery(id+"F96.opExtrude","SWEPT_FACE",FACE,{"disambiguationData":[OSD([sQuery(id+"F95.wireOp",EDGE,"E183")])]})});
            extrude(context, id + "F100", {"entities" : qUnion([Q0, Q1, Q2]), "operationType" : NewBodyOperationType.REMOVE, "endBound" : BoundingType.THROUGH_ALL, "oppositeDirection" : true, "depth" : 25.4 * mm, "offsetDistance" : 25.4 * mm});
        }
        {
            var Q0;
            Q0=makeQuery(id+"F93.opExtrude","SWEPT_FACE",FACE,{"disambiguationData":[OSD([sQuery(id+"F92.wireOp",EDGE,"E164")])]});
            var sketch = newSketch(context, id + "F101", { "sketchPlane" : qUnion([Q0])});
            skLineSegment(sketch, "E185.bottom", {"start": v(46.8, -126.66) * mm, "end": v(44.42, -126.66) * mm});
            skLineSegment(sketch, "E185.top", {"start": v(46.8, -104.43) * mm, "end": v(44.42, -104.43) * mm});
            skLineSegment(sketch, "E185.left", {"start": v(46.8, -126.66) * mm, "end": v(46.8, -104.43) * mm});
            skLineSegment(sketch, "E185.right", {"start": v(44.42, -126.66) * mm, "end": v(44.42, -104.43) * mm});
            skLineSegment(sketch, "E186.bottom", {"start": v(106.05, -126.66) * mm, "end": v(108.44, -126.66) * mm});
            skLineSegment(sketch, "E186.top", {"start": v(106.05, -104.43) * mm, "end": v(108.44, -104.43) * mm});
            skLineSegment(sketch, "E186.left", {"start": v(106.05, -126.66) * mm, "end": v(106.05, -104.43) * mm});
            skLineSegment(sketch, "E186.right", {"start": v(108.44, -126.66) * mm, "end": v(108.44, -104.43) * mm});
            skLineSegment(sketch, "E187.bottom", {"start": v(190.06, -126.66) * mm, "end": v(187.68, -126.66) * mm});
            skLineSegment(sketch, "E187.top", {"start": v(190.06, -104.43) * mm, "end": v(187.68, -104.43) * mm});
            skLineSegment(sketch, "E187.left", {"start": v(190.06, -126.66) * mm, "end": v(190.06, -104.43) * mm});
            skLineSegment(sketch, "E187.right", {"start": v(187.68, -126.66) * mm, "end": v(187.68, -104.43) * mm});
            skLineSegment(sketch, "E188.bottom", {"start": v(247.48, -126.66) * mm, "end": v(249.87, -126.66) * mm});
            skLineSegment(sketch, "E188.top", {"start": v(247.48, -104.43) * mm, "end": v(249.87, -104.43) * mm});
            skLineSegment(sketch, "E188.left", {"start": v(247.48, -126.66) * mm, "end": v(247.48, -104.43) * mm});
            skLineSegment(sketch, "E188.right", {"start": v(249.87, -126.66) * mm, "end": v(249.87, -104.43) * mm});
            skLineSegment(sketch, "E189.bottom", {"start": v(270.26, -126.66) * mm, "end": v(267.87, -126.66) * mm});
            skLineSegment(sketch, "E189.top", {"start": v(270.26, -104.43) * mm, "end": v(267.87, -104.43) * mm});
            skLineSegment(sketch, "E189.left", {"start": v(270.26, -126.66) * mm, "end": v(270.26, -104.43) * mm});
            skLineSegment(sketch, "E189.right", {"start": v(267.87, -126.66) * mm, "end": v(267.87, -104.43) * mm});
            skLineSegment(sketch, "E190.bottom", {"start": v(314.33, -126.66) * mm, "end": v(311.94, -126.66) * mm});
            skLineSegment(sketch, "E190.top", {"start": v(314.33, -104.43) * mm, "end": v(311.94, -104.43) * mm});
            skLineSegment(sketch, "E190.left", {"start": v(314.33, -126.66) * mm, "end": v(314.33, -104.43) * mm});
            skLineSegment(sketch, "E190.right", {"start": v(311.94, -126.66) * mm, "end": v(311.94, -104.43) * mm});
            skSolve(sketch);
        }
        {
            var Q0;
            Q0=makeQuery(id+"F101.imprint","IMPRINT",FACE,{"disambiguationData":[TD([[makeQuery(id+"F101.imprint","IMPRINT",EDGE,{"derivedFrom":sQuery(id+"F101.wireOp",EDGE,"E185.bottom")}),-1.0]])]});
            var Q1;
            Q1=makeQuery(id+"F101.imprint","IMPRINT",FACE,{"disambiguationData":[TD([[makeQuery(id+"F101.imprint","IMPRINT",EDGE,{"derivedFrom":sQuery(id+"F101.wireOp",EDGE,"E186.bottom")}),-1.0]])]});
            var Q2;
            Q2=makeQuery(id+"F101.imprint","IMPRINT",FACE,{"disambiguationData":[TD([[makeQuery(id+"F101.imprint","IMPRINT",EDGE,{"derivedFrom":sQuery(id+"F101.wireOp",EDGE,"E187.bottom")}),-1.0]])]});
            var Q3;
            Q3=makeQuery(id+"F101.imprint","IMPRINT",FACE,{"disambiguationData":[TD([[makeQuery(id+"F101.imprint","IMPRINT",EDGE,{"derivedFrom":sQuery(id+"F101.wireOp",EDGE,"E188.bottom")}),-1.0]])]});
            var Q4;
            Q4=makeQuery(id+"F101.imprint","IMPRINT",FACE,{"disambiguationData":[TD([[makeQuery(id+"F101.imprint","IMPRINT",EDGE,{"derivedFrom":sQuery(id+"F101.wireOp",EDGE,"E189.bottom")}),-1.0]])]});
            var Q5;
            Q5=makeQuery(id+"F101.imprint","IMPRINT",FACE,{"disambiguationData":[TD([[makeQuery(id+"F101.imprint","IMPRINT",EDGE,{"derivedFrom":sQuery(id+"F101.wireOp",EDGE,"E190.bottom")}),-1.0]])]});
            extrude(context, id + "F102", {"entities" : qUnion([Q0, Q1, Q2, Q3, Q4, Q5]), "operationType" : NewBodyOperationType.ADD, "depth" : 1.59 * mm, "offsetDistance" : 25.4 * mm});
        }
        {
            var Q0;
            Q0=makeQuery(id+"F93.opExtrude","SWEPT_FACE",FACE,{"disambiguationData":[OSD([sQuery(id+"F92.wireOp",EDGE,"E164")])]});
            var sketch = newSketch(context, id + "F103", { "sketchPlane" : qUnion([Q0])});
            skLineSegment(sketch, "E191.bottom", {"start": v(108.44, -126.66) * mm, "end": v(187.68, -126.66) * mm});
            skLineSegment(sketch, "E191.top", {"start": v(108.44, -80.62) * mm, "end": v(187.68, -80.62) * mm});
            skLineSegment(sketch, "E191.left", {"start": v(108.44, -126.66) * mm, "end": v(108.44, -80.62) * mm});
            skLineSegment(sketch, "E191.right", {"start": v(187.68, -126.66) * mm, "end": v(187.68, -80.62) * mm});
            skLineSegment(sketch, "E192.bottom", {"start": v(249.87, -126.66) * mm, "end": v(267.87, -126.66) * mm});
            skLineSegment(sketch, "E192.top", {"start": v(249.87, -80.62) * mm, "end": v(267.87, -80.62) * mm});
            skLineSegment(sketch, "E192.left", {"start": v(249.87, -126.66) * mm, "end": v(249.87, -80.62) * mm});
            skLineSegment(sketch, "E192.right", {"start": v(267.87, -126.66) * mm, "end": v(267.87, -80.62) * mm});
            skLineSegment(sketch, "E193.bottom", {"start": v(44.42, -126.66) * mm, "end": v(9.53, -126.66) * mm});
            skLineSegment(sketch, "E193.top", {"start": v(44.42, -80.62) * mm, "end": v(9.53, -80.62) * mm});
            skLineSegment(sketch, "E193.left", {"start": v(44.42, -126.66) * mm, "end": v(44.42, -80.62) * mm});
            skLineSegment(sketch, "E193.right", {"start": v(9.53, -126.66) * mm, "end": v(9.53, -80.62) * mm});
            skSolve(sketch);
        }
        {
            var Q0;
            {var subQ5=sQuery(id+"F103.wireOp",EDGE,"E193.bottom");Q0=makeQuery(id+"F103.imprint","IMPRINT",FACE,{"disambiguationData":[TD([[makeQuery(id+"F103.imprint","IMPRINT",EDGE,{"derivedFrom":subQ5}),-1.0]])]});}
            var Q1;
            {var subQ6=sQuery(id+"F103.wireOp",EDGE,"E191.bottom");Q1=makeQuery(id+"F103.imprint","IMPRINT",FACE,{"disambiguationData":[TD([[makeQuery(id+"F103.imprint","IMPRINT",EDGE,{"derivedFrom":subQ6}),-1.0]])]});}
            var Q2;
            {var subQ6=sQuery(id+"F103.wireOp",EDGE,"E192.bottom");Q2=makeQuery(id+"F103.imprint","IMPRINT",FACE,{"disambiguationData":[TD([[makeQuery(id+"F103.imprint","IMPRINT",EDGE,{"derivedFrom":subQ6}),-1.0]])]});}
            extrude(context, id + "F104", {"entities" : qUnion([Q0, Q1, Q2]), "operationType" : NewBodyOperationType.ADD, "depth" : 0.8 * mm, "offsetDistance" : 25.4 * mm});
        }
        {
            var Q0;
            Q0=makeQuery(id+"F102.opExtrude","CAP_EDGE",EDGE,{"disambiguationData":[OSD([sQuery(id+"F101.wireOp",EDGE,"E185.left")])],"isStart":false});
            var Q1;
            Q1=makeQuery(id+"F102.opExtrude","CAP_EDGE",EDGE,{"disambiguationData":[OSD([sQuery(id+"F101.wireOp",EDGE,"E185.left")])],"isStart":true});
            var Q2;
            Q2=makeQuery(id+"F102.opExtrude","CAP_EDGE",EDGE,{"disambiguationData":[OSD([sQuery(id+"F101.wireOp",EDGE,"E185.right")])],"isStart":false});
            var Q3;
            Q3=makeQuery(id+"F104.opExtrude","CAP_EDGE",EDGE,{"disambiguationData":[OSD([sQuery(id+"F103.wireOp",EDGE,"E193.top")])],"isStart":false});
            var Q4;
            Q4=makeQuery(id+"F104.opExtrude","CAP_EDGE",EDGE,{"disambiguationData":[OSD([sQuery(id+"F103.wireOp",EDGE,"E193.right")])],"isStart":false});
            var Q5;
            {var subQ0=sQuery(id+"F92.wireOp",EDGE,"E164");Q5=makeQuery(id+"F104.boolean.opBoolean","MERGE",EDGE,{"derivedFrom":[makeQuery(id+"F94.opFillet","BLEND_EDGE",EDGE,{"blendedFrom":[makeQuery(id+"F93.opExtrude","CAP_EDGE",EDGE,{"disambiguationData":[OSD([subQ0])],"isStart":true}),makeQuery(id+"F93.opExtrude","SWEPT_FACE",FACE,{"disambiguationData":[OSD([subQ0])]})],"blendedInto":[makeQuery(id+"F93.opExtrude","SWEPT_FACE",FACE,{"disambiguationData":[OSD([subQ0])]})]}),makeQuery(id+"F104.opExtrude","CAP_EDGE",EDGE,{"disambiguationData":[OSD([sQuery(id+"F103.wireOp",EDGE,"E193.right")])],"isStart":true})]});}
            var Q6;
            Q6=makeQuery(id+"F104.opExtrude","CAP_EDGE",EDGE,{"disambiguationData":[OSD([sQuery(id+"F103.wireOp",EDGE,"E193.bottom")])],"isStart":false});
            var Q7;
            Q7=makeQuery(id+"F102.opExtrude","CAP_EDGE",EDGE,{"disambiguationData":[OSD([sQuery(id+"F101.wireOp",EDGE,"E186.left")])],"isStart":true});
            var Q8;
            Q8=makeQuery(id+"F102.opExtrude","CAP_EDGE",EDGE,{"disambiguationData":[OSD([sQuery(id+"F101.wireOp",EDGE,"E186.left")])],"isStart":false});
            var Q9;
            Q9=makeQuery(id+"F102.opExtrude","CAP_EDGE",EDGE,{"disambiguationData":[OSD([sQuery(id+"F101.wireOp",EDGE,"E186.right")])],"isStart":false});
            var Q10;
            Q10=makeQuery(id+"F102.opExtrude","CAP_EDGE",EDGE,{"disambiguationData":[OSD([sQuery(id+"F101.wireOp",EDGE,"E187.right")])],"isStart":false});
            var Q11;
            Q11=makeQuery(id+"F102.opExtrude","CAP_EDGE",EDGE,{"disambiguationData":[OSD([sQuery(id+"F101.wireOp",EDGE,"E187.left")])],"isStart":false});
            var Q12;
            Q12=makeQuery(id+"F102.opExtrude","CAP_EDGE",EDGE,{"disambiguationData":[OSD([sQuery(id+"F101.wireOp",EDGE,"E187.left")])],"isStart":true});
            var Q13;
            Q13=makeQuery(id+"F102.opExtrude","CAP_EDGE",EDGE,{"disambiguationData":[OSD([sQuery(id+"F101.wireOp",EDGE,"E189.left")])],"isStart":true});
            var Q14;
            Q14=makeQuery(id+"F102.opExtrude","CAP_EDGE",EDGE,{"disambiguationData":[OSD([sQuery(id+"F101.wireOp",EDGE,"E189.left")])],"isStart":false});
            var Q15;
            {var subQ0=sQuery(id+"F103.wireOp",EDGE,"E192.left");Q15=makeQuery(id+"F104.boolean.opBoolean","SPLIT",EDGE,{"disambiguationData":[topologyDisambiguationEdgeConnected([makeQuery(id+"F102.opExtrude","SWEPT_FACE",FACE,{"disambiguationData":[OSD([sQuery(id+"F101.wireOp",EDGE,"E188.right")])]})])],"derivedFrom":makeQuery(id+"F104.opExtrude","CAP_EDGE",EDGE,{"disambiguationData":[OSD([subQ0])],"isStart":false})});}
            var Q16;
            Q16=makeQuery(id+"F102.opExtrude","CAP_EDGE",EDGE,{"disambiguationData":[OSD([sQuery(id+"F101.wireOp",EDGE,"E188.right")])],"isStart":false});
            var Q17;
            Q17=makeQuery(id+"F102.opExtrude","CAP_EDGE",EDGE,{"disambiguationData":[OSD([sQuery(id+"F101.wireOp",EDGE,"E189.right")])],"isStart":false});
            var Q18;
            Q18=makeQuery(id+"F102.opExtrude","CAP_EDGE",EDGE,{"disambiguationData":[OSD([sQuery(id+"F101.wireOp",EDGE,"E188.left")])],"isStart":true});
            var Q19;
            Q19=makeQuery(id+"F102.opExtrude","CAP_EDGE",EDGE,{"disambiguationData":[OSD([sQuery(id+"F101.wireOp",EDGE,"E188.left")])],"isStart":false});
            var Q20;
            {var subQ0=sQuery(id+"F103.wireOp",EDGE,"E192.right");Q20=makeQuery(id+"F104.boolean.opBoolean","SPLIT",EDGE,{"disambiguationData":[topologyDisambiguationEdgeConnected([makeQuery(id+"F102.opExtrude","SWEPT_FACE",FACE,{"disambiguationData":[OSD([sQuery(id+"F101.wireOp",EDGE,"E189.right")])]})])],"derivedFrom":makeQuery(id+"F104.opExtrude","CAP_EDGE",EDGE,{"disambiguationData":[OSD([subQ0])],"isStart":false})});}
            var Q21;
            Q21=makeQuery(id+"F102.opExtrude","CAP_EDGE",EDGE,{"disambiguationData":[OSD([sQuery(id+"F101.wireOp",EDGE,"E190.right")])],"isStart":true});
            var Q22;
            Q22=makeQuery(id+"F102.opExtrude","CAP_EDGE",EDGE,{"disambiguationData":[OSD([sQuery(id+"F101.wireOp",EDGE,"E190.right")])],"isStart":false});
            var Q23;
            Q23=makeQuery(id+"F102.opExtrude","CAP_EDGE",EDGE,{"disambiguationData":[OSD([sQuery(id+"F101.wireOp",EDGE,"E190.left")])],"isStart":false});
            var Q24;
            {var subQ0=sQuery(id+"F92.wireOp",EDGE,"E164");Q24=makeQuery(id+"F102.boolean.opBoolean","MERGE",EDGE,{"derivedFrom":[makeQuery(id+"F94.opFillet","BLEND_EDGE",EDGE,{"blendedFrom":[makeQuery(id+"F93.opExtrude","CAP_EDGE",EDGE,{"disambiguationData":[OSD([subQ0])],"isStart":false}),makeQuery(id+"F93.opExtrude","SWEPT_FACE",FACE,{"disambiguationData":[OSD([subQ0])]})],"blendedInto":[makeQuery(id+"F93.opExtrude","SWEPT_FACE",FACE,{"disambiguationData":[OSD([subQ0])]})]}),makeQuery(id+"F102.opExtrude","CAP_EDGE",EDGE,{"disambiguationData":[OSD([sQuery(id+"F101.wireOp",EDGE,"E190.left")])],"isStart":true})]});}
            var Q25;
            {var subQ0=sQuery(id+"F103.wireOp",EDGE,"E191.left");Q25=makeQuery(id+"F104.boolean.opBoolean","SPLIT",EDGE,{"disambiguationData":[topologyDisambiguationEdgeConnected([makeQuery(id+"F102.opExtrude","SWEPT_FACE",FACE,{"disambiguationData":[OSD([sQuery(id+"F101.wireOp",EDGE,"E186.right")])]})])],"derivedFrom":makeQuery(id+"F104.opExtrude","CAP_EDGE",EDGE,{"disambiguationData":[OSD([subQ0])],"isStart":false})});}
            var Q26;
            {var subQ0=sQuery(id+"F103.wireOp",EDGE,"E193.left");Q26=makeQuery(id+"F104.boolean.opBoolean","SPLIT",EDGE,{"disambiguationData":[topologyDisambiguationEdgeConnected([makeQuery(id+"F102.opExtrude","SWEPT_FACE",FACE,{"disambiguationData":[OSD([sQuery(id+"F101.wireOp",EDGE,"E185.right")])]})])],"derivedFrom":makeQuery(id+"F104.opExtrude","CAP_EDGE",EDGE,{"disambiguationData":[OSD([subQ0])],"isStart":false})});}
            fillet(context, id + "F105", {"entities" : qUnion([Q0, Q1, Q2, Q3, Q4, Q5, Q6, Q7, Q8, Q9, Q10, Q11, Q12, Q13, Q14, Q15, Q16, Q17, Q18, Q19, Q20, Q21, Q22, Q23, Q24, Q25, Q26]), "radius" : 0.25 * mm, "tangentPropagation" : true, "allowEdgeOverflow" : false});
        }
        {
            var Q0;
            {var subQ0=sQuery(id+"F6.wireOp",EDGE,"E9");var subQ1=sQuery(id+"F0.wireOp",EDGE,"E0.right");var subQ2=sQuery(id+"F0.wireOp",EDGE,"E0.bottom");var subQ3=sQuery(id+"F0.wireOp",EDGE,"E0.left");var subQ4=sQuery(id+"F0.wireOp",EDGE,"E0.top");var subQ5=sQuery(id+"F6.wireOp",EDGE,"E17");var subQ6=sQuery(id+"F4.wireOp",EDGE,"E8.0");var subQ7=sQuery(id+"F4.wireOp",EDGE,"E3.0");var subQ8=sQuery(id+"F4.wireOp",EDGE,"E2.0");var subQ9=sQuery(id+"F4.wireOp",EDGE,"E7.0");var subQ10=sQuery(id+"F4.wireOp",EDGE,"E6.0");var subQ11=sQuery(id+"F4.wireOp",EDGE,"E4.0");var subQ12=sQuery(id+"F4.wireOp",EDGE,"E5.0");var subQ13=sQuery(id+"F4.wireOp",EDGE,"E1.0");Q0=makeQuery(id+"F68.boolean.opBoolean","SPLIT",FACE,{"disambiguationData":[TD([makeQuery(id+"F5.opExtrude","SWEPT_FACE",FACE,{"disambiguationData":[OSD([subQ8])]})])],"derivedFrom":makeQuery(id+"F11.boolean.opBoolean","MERGE",FACE,{"derivedFrom":[makeQuery(id+"F7.boolean.opBoolean","MERGE",FACE,{"derivedFrom":[makeQuery(id+"F5.opExtrude","CAP_FACE",FACE,{"disambiguationData":[OSD([subQ2,subQ4,subQ3,subQ1,subQ13,subQ8,subQ7,subQ11,subQ12,subQ10,subQ9,subQ6])],"isStart":false}),makeQuery(id+"F7.opExtrude","CAP_FACE",FACE,{"disambiguationData":[OSD([subQ8,subQ7,subQ0])],"isStart":false}),makeQuery(id+"F7.opExtrude","CAP_FACE",FACE,{"disambiguationData":[OSD([subQ13,subQ7,sQuery(id+"F6.wireOp",EDGE,"E11")])],"isStart":false}),makeQuery(id+"F7.opExtrude","CAP_FACE",FACE,{"disambiguationData":[OSD([subQ12,subQ10,sQuery(id+"F6.wireOp",EDGE,"E12")])],"isStart":false}),makeQuery(id+"F7.opExtrude","CAP_FACE",FACE,{"disambiguationData":[OSD([subQ11,subQ10,sQuery(id+"F6.wireOp",EDGE,"E13")])],"isStart":false}),makeQuery(id+"F7.opExtrude","CAP_FACE",FACE,{"disambiguationData":[OSD([subQ9,sQuery(id+"F6.wireOp",EDGE,"E14")])],"isStart":false}),makeQuery(id+"F7.opExtrude","CAP_FACE",FACE,{"disambiguationData":[OSD([subQ9,sQuery(id+"F6.wireOp",EDGE,"E15")])],"isStart":false}),makeQuery(id+"F7.opExtrude","CAP_FACE",FACE,{"disambiguationData":[OSD([subQ6,sQuery(id+"F6.wireOp",EDGE,"E16")])],"isStart":false}),makeQuery(id+"F7.opExtrude","CAP_FACE",FACE,{"disambiguationData":[OSD([subQ6,subQ5])],"isStart":false})]}),makeQuery(id+"F11.opExtrude","CAP_FACE",FACE,{"disambiguationData":[OSD([sQuery(id+"F10.wireOp",EDGE,"E26"),sQuery(id+"F10.wireOp",EDGE,"E27"),sQuery(id+"F10.wireOp",EDGE,"E28"),sQuery(id+"F10.wireOp",EDGE,"E29")])],"isStart":false}),makeQuery(id+"F11.opExtrude","CAP_FACE",FACE,{"disambiguationData":[OSD([sQuery(id+"F10.wireOp",EDGE,"E34"),sQuery(id+"F10.wireOp",EDGE,"E35"),sQuery(id+"F10.wireOp",EDGE,"E36"),sQuery(id+"F10.wireOp",EDGE,"E37")])],"isStart":false}),makeQuery(id+"F11.opExtrude","CAP_FACE",FACE,{"disambiguationData":[OSD([sQuery(id+"F10.wireOp",EDGE,"E42"),sQuery(id+"F10.wireOp",EDGE,"E43"),sQuery(id+"F10.wireOp",EDGE,"E44"),sQuery(id+"F10.wireOp",EDGE,"E45")])],"isStart":false}),makeQuery(id+"F11.opExtrude","CAP_FACE",FACE,{"disambiguationData":[OSD([sQuery(id+"F10.wireOp",EDGE,"E47"),sQuery(id+"F10.wireOp",EDGE,"E48"),sQuery(id+"F10.wireOp",EDGE,"E49"),sQuery(id+"F10.wireOp",EDGE,"E50")])],"isStart":false})]})});}
            var Q1;
            Q1=makeQuery(id+"F44.opExtrude","CAP_FACE",FACE,{"disambiguationData":[OSD([sQuery(id+"F43.wireOp",EDGE,"E84.bottom"),sQuery(id+"F43.wireOp",EDGE,"E84.top"),sQuery(id+"F43.wireOp",EDGE,"E84.left"),sQuery(id+"F43.wireOp",EDGE,"E84.right"),sQuery(id+"F43.wireOp",EDGE,"E85.top"),sQuery(id+"F43.wireOp",EDGE,"E85.left"),sQuery(id+"F43.wireOp",EDGE,"E85.right"),sQuery(id+"F43.wireOp",EDGE,"E86.trimOffspring")])],"isStart":false});
            var Q2;
            Q2=makeQuery(id+"F39.opExtrude","CAP_FACE",FACE,{"disambiguationData":[OSD([sQuery(id+"F38.wireOp",EDGE,"E82.bottom"),sQuery(id+"F38.wireOp",EDGE,"E82.top"),sQuery(id+"F38.wireOp",EDGE,"E82.left"),sQuery(id+"F38.wireOp",EDGE,"E82.right")])],"isStart":false});
            var Q3;
            Q3=makeQuery(id+"F56.opExtrude","CAP_FACE",FACE,{"disambiguationData":[OSD([sQuery(id+"F55.wireOp",EDGE,"E102.bottom"),sQuery(id+"F55.wireOp",EDGE,"E102.top"),sQuery(id+"F55.wireOp",EDGE,"E103"),sQuery(id+"F55.wireOp",EDGE,"E104"),sQuery(id+"F55.wireOp",EDGE,"E105"),sQuery(id+"F55.wireOp",EDGE,"E106")])],"isStart":false});
            var Q4;
            Q4=makeQuery(id+"F27.opExtrude","CAP_FACE",FACE,{"disambiguationData":[OSD([sQuery(id+"F26.wireOp",EDGE,"E60.bottom"),sQuery(id+"F26.wireOp",EDGE,"E60.top"),sQuery(id+"F26.wireOp",EDGE,"E60.left"),sQuery(id+"F26.wireOp",EDGE,"E60.right")])],"isStart":false});
            var Q5;
            Q5=makeQuery(id+"F22.opExtrude","CAP_FACE",FACE,{"disambiguationData":[OSD([sQuery(id+"F21.wireOp",EDGE,"E56.bottom"),sQuery(id+"F21.wireOp",EDGE,"E56.top"),sQuery(id+"F21.wireOp",EDGE,"E56.left"),sQuery(id+"F21.wireOp",EDGE,"E56.right")])],"isStart":false});
            var Q6;
            {var subQ0=sQuery(id+"F6.wireOp",EDGE,"E13");var subQ1=sQuery(id+"F0.wireOp",EDGE,"E0.bottom");var subQ2=sQuery(id+"F0.wireOp",EDGE,"E0.right");var subQ3=sQuery(id+"F0.wireOp",EDGE,"E0.left");var subQ4=sQuery(id+"F0.wireOp",EDGE,"E0.top");var subQ5=sQuery(id+"F4.wireOp",EDGE,"E8.0");var subQ6=sQuery(id+"F4.wireOp",EDGE,"E6.0");var subQ7=sQuery(id+"F4.wireOp",EDGE,"E4.0");var subQ8=sQuery(id+"F6.wireOp",EDGE,"E16");var subQ9=sQuery(id+"F4.wireOp",EDGE,"E7.0");var subQ10=sQuery(id+"F4.wireOp",EDGE,"E5.0");var subQ11=sQuery(id+"F4.wireOp",EDGE,"E3.0");var subQ12=sQuery(id+"F4.wireOp",EDGE,"E1.0");var subQ13=sQuery(id+"F4.wireOp",EDGE,"E2.0");Q6=makeQuery(id+"F68.boolean.opBoolean","SPLIT",FACE,{"disambiguationData":[TD([makeQuery(id+"F5.opExtrude","SWEPT_FACE",FACE,{"disambiguationData":[OSD([subQ7])]})])],"derivedFrom":makeQuery(id+"F11.boolean.opBoolean","MERGE",FACE,{"derivedFrom":[makeQuery(id+"F7.boolean.opBoolean","MERGE",FACE,{"derivedFrom":[makeQuery(id+"F5.opExtrude","CAP_FACE",FACE,{"disambiguationData":[OSD([subQ1,subQ4,subQ3,subQ2,subQ12,subQ13,subQ11,subQ7,subQ10,subQ6,subQ9,subQ5])],"isStart":false}),makeQuery(id+"F7.opExtrude","CAP_FACE",FACE,{"disambiguationData":[OSD([subQ13,subQ11,sQuery(id+"F6.wireOp",EDGE,"E9")])],"isStart":false}),makeQuery(id+"F7.opExtrude","CAP_FACE",FACE,{"disambiguationData":[OSD([subQ12,subQ11,sQuery(id+"F6.wireOp",EDGE,"E11")])],"isStart":false}),makeQuery(id+"F7.opExtrude","CAP_FACE",FACE,{"disambiguationData":[OSD([subQ10,subQ6,sQuery(id+"F6.wireOp",EDGE,"E12")])],"isStart":false}),makeQuery(id+"F7.opExtrude","CAP_FACE",FACE,{"disambiguationData":[OSD([subQ7,subQ6,subQ0])],"isStart":false}),makeQuery(id+"F7.opExtrude","CAP_FACE",FACE,{"disambiguationData":[OSD([subQ9,sQuery(id+"F6.wireOp",EDGE,"E14")])],"isStart":false}),makeQuery(id+"F7.opExtrude","CAP_FACE",FACE,{"disambiguationData":[OSD([subQ9,sQuery(id+"F6.wireOp",EDGE,"E15")])],"isStart":false}),makeQuery(id+"F7.opExtrude","CAP_FACE",FACE,{"disambiguationData":[OSD([subQ5,subQ8])],"isStart":false}),makeQuery(id+"F7.opExtrude","CAP_FACE",FACE,{"disambiguationData":[OSD([subQ5,sQuery(id+"F6.wireOp",EDGE,"E17")])],"isStart":false})]}),makeQuery(id+"F11.opExtrude","CAP_FACE",FACE,{"disambiguationData":[OSD([sQuery(id+"F10.wireOp",EDGE,"E26"),sQuery(id+"F10.wireOp",EDGE,"E27"),sQuery(id+"F10.wireOp",EDGE,"E28"),sQuery(id+"F10.wireOp",EDGE,"E29")])],"isStart":false}),makeQuery(id+"F11.opExtrude","CAP_FACE",FACE,{"disambiguationData":[OSD([sQuery(id+"F10.wireOp",EDGE,"E34"),sQuery(id+"F10.wireOp",EDGE,"E35"),sQuery(id+"F10.wireOp",EDGE,"E36"),sQuery(id+"F10.wireOp",EDGE,"E37")])],"isStart":false}),makeQuery(id+"F11.opExtrude","CAP_FACE",FACE,{"disambiguationData":[OSD([sQuery(id+"F10.wireOp",EDGE,"E42"),sQuery(id+"F10.wireOp",EDGE,"E43"),sQuery(id+"F10.wireOp",EDGE,"E44"),sQuery(id+"F10.wireOp",EDGE,"E45")])],"isStart":false}),makeQuery(id+"F11.opExtrude","CAP_FACE",FACE,{"disambiguationData":[OSD([sQuery(id+"F10.wireOp",EDGE,"E47"),sQuery(id+"F10.wireOp",EDGE,"E48"),sQuery(id+"F10.wireOp",EDGE,"E49"),sQuery(id+"F10.wireOp",EDGE,"E50")])],"isStart":false})]})});}
            var Q7;
            {var subQ0=sQuery(id+"F6.wireOp",EDGE,"E14");var subQ1=sQuery(id+"F10.wireOp",EDGE,"E26");var subQ2=sQuery(id+"F6.wireOp",EDGE,"E12");var subQ3=sQuery(id+"F0.wireOp",EDGE,"E0.right");var subQ4=sQuery(id+"F6.wireOp",EDGE,"E11");var subQ5=sQuery(id+"F0.wireOp",EDGE,"E0.left");var subQ6=sQuery(id+"F0.wireOp",EDGE,"E0.top");var subQ7=sQuery(id+"F0.wireOp",EDGE,"E0.bottom");var subQ9=sQuery(id+"F4.wireOp",EDGE,"E6.0");var subQ10=sQuery(id+"F6.wireOp",EDGE,"E15");var subQ11=sQuery(id+"F10.wireOp",EDGE,"E27");var subQ12=sQuery(id+"F4.wireOp",EDGE,"E5.0");var subQ13=sQuery(id+"F4.wireOp",EDGE,"E1.0");var subQ14=sQuery(id+"F4.wireOp",EDGE,"E3.0");var subQ15=sQuery(id+"F4.wireOp",EDGE,"E7.0");var subQ16=sQuery(id+"F10.wireOp",EDGE,"E43");var subQ17=sQuery(id+"F10.wireOp",EDGE,"E28");var subQ18=sQuery(id+"F10.wireOp",EDGE,"E34");var subQ19=sQuery(id+"F10.wireOp",EDGE,"E35");var subQ20=sQuery(id+"F10.wireOp",EDGE,"E36");var subQ21=sQuery(id+"F10.wireOp",EDGE,"E42");var subQ22=sQuery(id+"F10.wireOp",EDGE,"E44");var subQ23=sQuery(id+"F10.wireOp",EDGE,"E47");var subQ26=sQuery(id+"F10.wireOp",EDGE,"E48");var subQ27=sQuery(id+"F10.wireOp",EDGE,"E49");var subQ28=sQuery(id+"F4.wireOp",EDGE,"E8.0");var subQ29=sQuery(id+"F4.wireOp",EDGE,"E4.0");var subQ30=sQuery(id+"F4.wireOp",EDGE,"E2.0");Q7=makeQuery(id+"F68.boolean.opBoolean","SPLIT",FACE,{"disambiguationData":[TD([makeQuery(id+"F1.opExtrude","SWEPT_FACE",FACE,{"disambiguationData":[OSD([subQ6])]})])],"derivedFrom":makeQuery(id+"F11.boolean.opBoolean","MERGE",FACE,{"derivedFrom":[makeQuery(id+"F7.boolean.opBoolean","MERGE",FACE,{"derivedFrom":[makeQuery(id+"F5.opExtrude","CAP_FACE",FACE,{"disambiguationData":[OSD([subQ7,subQ6,subQ5,subQ3,subQ13,subQ30,subQ14,subQ29,subQ12,subQ9,subQ15,subQ28])],"isStart":false}),makeQuery(id+"F7.opExtrude","CAP_FACE",FACE,{"disambiguationData":[OSD([subQ30,subQ14,sQuery(id+"F6.wireOp",EDGE,"E9")])],"isStart":false}),makeQuery(id+"F7.opExtrude","CAP_FACE",FACE,{"disambiguationData":[OSD([subQ13,subQ14,subQ4])],"isStart":false}),makeQuery(id+"F7.opExtrude","CAP_FACE",FACE,{"disambiguationData":[OSD([subQ12,subQ9,subQ2])],"isStart":false}),makeQuery(id+"F7.opExtrude","CAP_FACE",FACE,{"disambiguationData":[OSD([subQ29,subQ9,sQuery(id+"F6.wireOp",EDGE,"E13")])],"isStart":false}),makeQuery(id+"F7.opExtrude","CAP_FACE",FACE,{"disambiguationData":[OSD([subQ15,subQ0])],"isStart":false}),makeQuery(id+"F7.opExtrude","CAP_FACE",FACE,{"disambiguationData":[OSD([subQ15,subQ10])],"isStart":false}),makeQuery(id+"F7.opExtrude","CAP_FACE",FACE,{"disambiguationData":[OSD([subQ28,sQuery(id+"F6.wireOp",EDGE,"E16")])],"isStart":false}),makeQuery(id+"F7.opExtrude","CAP_FACE",FACE,{"disambiguationData":[OSD([subQ28,sQuery(id+"F6.wireOp",EDGE,"E17")])],"isStart":false})]}),makeQuery(id+"F11.opExtrude","CAP_FACE",FACE,{"disambiguationData":[OSD([subQ1,subQ11,subQ17,sQuery(id+"F10.wireOp",EDGE,"E29")])],"isStart":false}),makeQuery(id+"F11.opExtrude","CAP_FACE",FACE,{"disambiguationData":[OSD([subQ18,subQ19,subQ20,sQuery(id+"F10.wireOp",EDGE,"E37")])],"isStart":false}),makeQuery(id+"F11.opExtrude","CAP_FACE",FACE,{"disambiguationData":[OSD([subQ21,subQ16,subQ22,sQuery(id+"F10.wireOp",EDGE,"E45")])],"isStart":false}),makeQuery(id+"F11.opExtrude","CAP_FACE",FACE,{"disambiguationData":[OSD([subQ23,subQ26,subQ27,sQuery(id+"F10.wireOp",EDGE,"E50")])],"isStart":false})]})});}
            fillet(context, id + "F106", {"entities" : qUnion([Q0, Q1, Q2, Q3, Q4, Q5, Q6, Q7]), "radius" : 0.25 * mm, "tangentPropagation" : true, "allowEdgeOverflow" : false});
        }
    });
